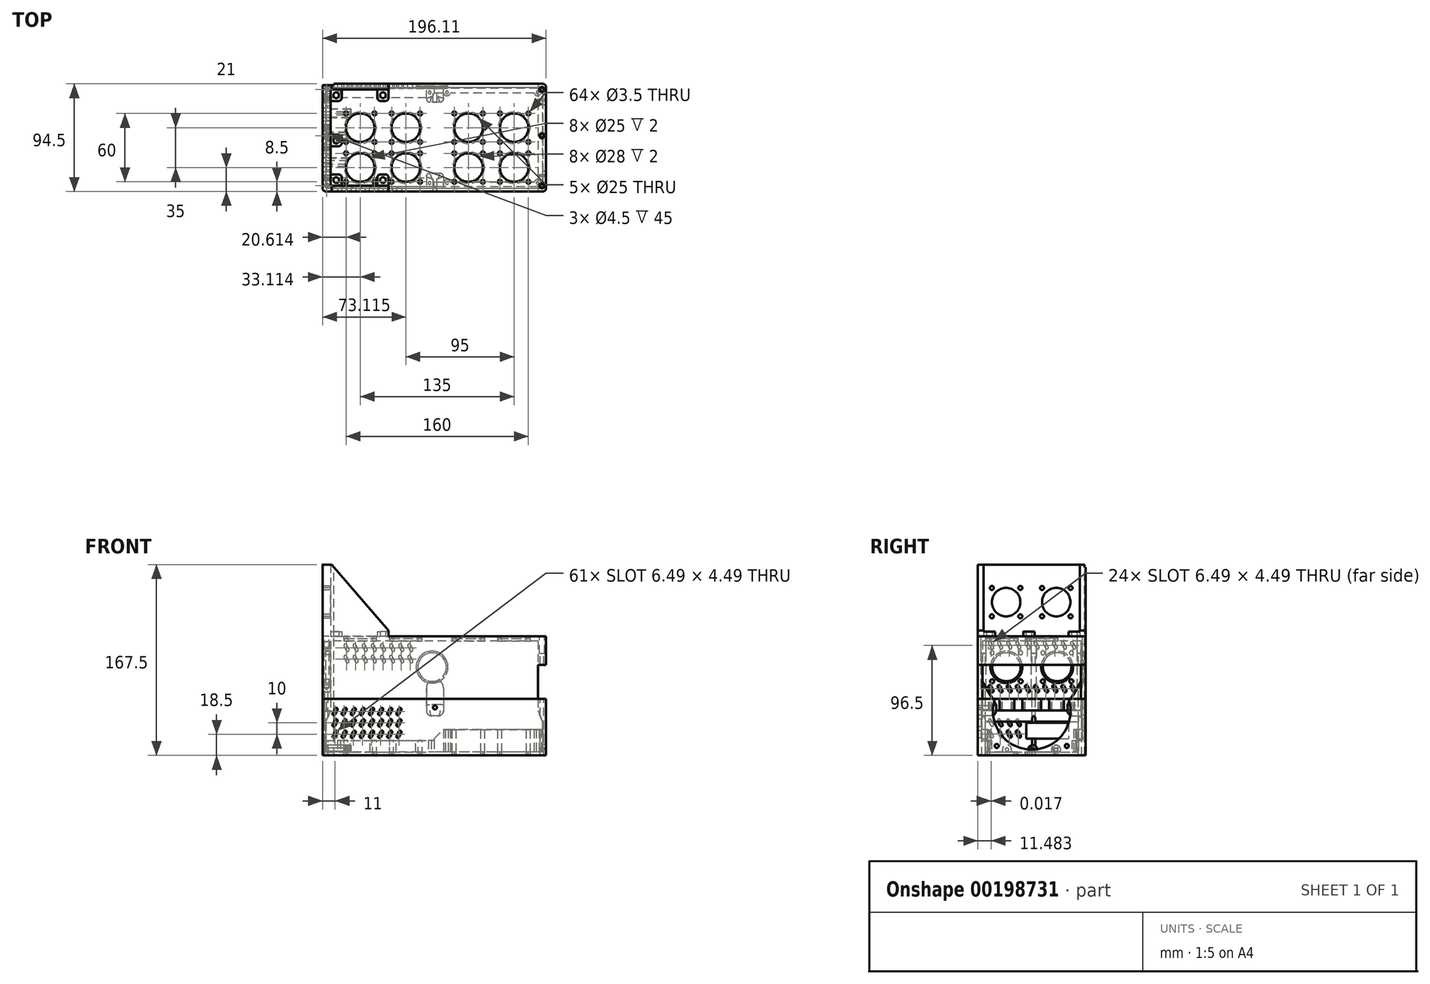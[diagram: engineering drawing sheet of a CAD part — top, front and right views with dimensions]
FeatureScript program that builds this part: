
annotation { "Feature Type Name" : "Feature", "Feature Type Description" : "" }
export const myFeature = defineFeature(function(context is Context, id is Id, definition is map)
    precondition{}
    {
        {
            var Q0;
            Q0=qCreatedBy(makeId("Top.planeOp"),FACE);
            var sketch = newSketch(context, id + "F0", { "sketchPlane" : qUnion([Q0])});
            skLineSegment(sketch, "E0.bottom", {"start": v(0, 0) * mm, "end": v(196, 0) * mm});
            skLineSegment(sketch, "E0.top", {"start": v(0, 94.5) * mm, "end": v(196, 94.5) * mm});
            skLineSegment(sketch, "E0.left", {"start": v(0, 0) * mm, "end": v(0, 94.5) * mm});
            skLineSegment(sketch, "E0.right", {"start": v(196, 0) * mm, "end": v(196, 94.5) * mm});
            skSolve(sketch);
        }
        {
            var Q0;
            Q0=qSketchRegion(id+"F0",true);
            extrude(context, id + "F1", {"entities" : qUnion([Q0]), "depth" : (3 + 10 + 36.5) * mm, "offsetDistance" : 25 * mm});
        }
        {
            var Q0;
            Q0=makeQuery(id+"F1.opExtrude","CAP_FACE",FACE,{"disambiguationData":[OSD([sQuery(id+"F0.wireOp",EDGE,"E0.bottom"),sQuery(id+"F0.wireOp",EDGE,"E0.top"),sQuery(id+"F0.wireOp",EDGE,"E0.left"),sQuery(id+"F0.wireOp",EDGE,"E0.right")])],"isStart":false});
            shell(context, id + "F2", {"entities" : qUnion([Q0]), "thickness" : 3 * mm});
        }
        {
            var Q0;
            Q0=makeQuery(id+"F2.opShell","OFFSET_FACE",FACE,{"disambiguationData":[OSD([sQuery(id+"F0.wireOp",EDGE,"E0.bottom"),sQuery(id+"F0.wireOp",EDGE,"E0.top"),sQuery(id+"F0.wireOp",EDGE,"E0.left"),sQuery(id+"F0.wireOp",EDGE,"E0.right")])]});
            var sketch = newSketch(context, id + "F3", { "sketchPlane" : qUnion([Q0])});
            skLineSegment(sketch, "E1.bottom", {"start": v(3, 3) * mm, "end": v(98, 3) * mm});
            skLineSegment(sketch, "E1.top", {"start": v(3, 12) * mm, "end": v(98, 12) * mm});
            skLineSegment(sketch, "E1.left", {"start": v(3, 3) * mm, "end": v(3, 12) * mm});
            skLineSegment(sketch, "E1.right", {"start": v(98, 3) * mm, "end": v(98, 12) * mm});
            skLineSegment(sketch, "E2.bottom", {"start": v(3, 91.5) * mm, "end": v(98, 91.5) * mm});
            skLineSegment(sketch, "E2.top", {"start": v(3, 82.5) * mm, "end": v(98, 82.5) * mm});
            skLineSegment(sketch, "E2.left", {"start": v(3, 91.5) * mm, "end": v(3, 82.5) * mm});
            skLineSegment(sketch, "E2.right", {"start": v(98, 91.5) * mm, "end": v(98, 82.5) * mm});
            skCircle(sketch, "E3", {"center": v(14.5, 87) * mm, "radius": 1.25 * mm});
            skCircle(sketch, "E4", {"center": v(94, 87) * mm, "radius": 1.25 * mm});
            skCircle(sketch, "E5", {"center": v(14.5, 7.5) * mm, "radius": 1.25 * mm});
            skCircle(sketch, "E6", {"center": v(94, 7.5) * mm, "radius": 1.25 * mm});
            skSolve(sketch);
        }
        {
            var Q0;
            Q0=qSketchRegion(id+"F3",true);
            extrude(context, id + "F4", {"entities" : qUnion([Q0]), "operationType" : NewBodyOperationType.ADD, "depth" : 10 * mm, "offsetDistance" : 25 * mm});
        }
        {
            var Q0;
            {var subQ0=sQuery(id+"F0.wireOp",EDGE,"E0.right");var subQ1=sQuery(id+"F0.wireOp",EDGE,"E0.left");var subQ2=sQuery(id+"F0.wireOp",EDGE,"E0.top");var subQ3=sQuery(id+"F0.wireOp",EDGE,"E0.bottom");Q0=makeQuery(id+"F4.boolean.opBoolean","SPLIT",FACE,{"disambiguationData":[TD([makeQuery(id+"F2.opShell","OFFSET_FACE",FACE,{"disambiguationData":[OSD([subQ3])]})])],"derivedFrom":makeQuery(id+"F2.opShell","OFFSET_FACE",FACE,{"disambiguationData":[OSD([subQ3,subQ2,subQ1,subQ0])]})});}
            var sketch = newSketch(context, id + "F5", { "sketchPlane" : qUnion([Q0])});
            skLineSegment(sketch, "E7.bottom", {"start": v(193, 3) * mm, "end": v(98, 3) * mm});
            skLineSegment(sketch, "E7.top", {"start": v(193, 8) * mm, "end": v(191.6, 8) * mm});
            skLineSegment(sketch, "E7.left", {"start": v(193, 3) * mm, "end": v(193, 8) * mm});
            skLineSegment(sketch, "E7.right", {"start": v(98, 3) * mm, "end": v(98, 8) * mm});
            skLineSegment(sketch, "E8.bottom", {"start": v(193, 91.5) * mm, "end": v(98, 91.5) * mm});
            skLineSegment(sketch, "E8.top", {"start": v(193, 86.5) * mm, "end": v(191.6, 86.5) * mm});
            skLineSegment(sketch, "E8.left", {"start": v(193, 91.5) * mm, "end": v(193, 86.5) * mm});
            skLineSegment(sketch, "E8.right", {"start": v(98, 91.5) * mm, "end": v(98, 86.5) * mm});
            skCircle(sketch, "E9", {"center": v(188.65, 87) * mm, "radius": 1.25 * mm});
            skCircle(sketch, "E10", {"center": v(109.15, 87) * mm, "radius": 1.25 * mm});
            skCircle(sketch, "E11", {"center": v(109.15, 7.5) * mm, "radius": 1.25 * mm});
            skCircle(sketch, "E12", {"center": v(188.65, 7.5) * mm, "radius": 1.25 * mm});
            skArc(sketch, "E13", {"start": v(106.2, 86.5) * mm, "mid": v(109.15, 84) * mm, "end": v(112.1, 86.5) * mm});
            skArc(sketch, "E14", {"start": v(185.7, 86.5) * mm, "mid": v(188.65, 84) * mm, "end": v(191.6, 86.5) * mm});
            skArc(sketch, "E15", {"start": v(112.1, 8) * mm, "mid": v(109.15, 10.5) * mm, "end": v(106.2, 8) * mm});
            skArc(sketch, "E16", {"start": v(191.6, 8) * mm, "mid": v(188.65, 10.5) * mm, "end": v(185.7, 8) * mm});
            skLineSegment(sketch, "E17.trimOffspring", {"start": v(106.2, 86.5) * mm, "end": v(98, 86.5) * mm});
            skLineSegment(sketch, "E18.trimOffspring", {"start": v(185.7, 86.5) * mm, "end": v(112.1, 86.5) * mm});
            skLineSegment(sketch, "E19.trimOffspring", {"start": v(185.7, 8) * mm, "end": v(112.1, 8) * mm});
            skLineSegment(sketch, "E20.trimOffspring", {"start": v(106.2, 8) * mm, "end": v(98, 8) * mm});
            skSolve(sketch);
        }
        {
            var Q0;
            Q0=qSketchRegion(id+"F5",true);
            extrude(context, id + "F6", {"entities" : qUnion([Q0]), "operationType" : NewBodyOperationType.ADD, "depth" : (10 + 1.6 + 8) * mm, "offsetDistance" : 25 * mm});
        }
        {
            var Q0;
            Q0=makeQuery(id+"F6.opExtrude","CAP_EDGE",EDGE,{"disambiguationData":[OSD([sQuery(id+"F5.wireOp",EDGE,"E8.right")])],"isStart":false});
            chamfer(context, id + "F7", {"entities" : qUnion([Q0]), "width" : 8 * mm, "tangentPropagation" : true});
        }
        {
            var Q0;
            Q0=makeQuery(id+"F6.opExtrude","CAP_EDGE",EDGE,{"disambiguationData":[OSD([sQuery(id+"F5.wireOp",EDGE,"E7.right")])],"isStart":false});
            chamfer(context, id + "F8", {"entities" : qUnion([Q0]), "width" : 8 * mm, "tangentPropagation" : true});
        }
        {
            var Q0;
            Q0=makeQuery(id+"F4.opExtrude","SWEPT_EDGE",EDGE,{"disambiguationData":[OSD([sQuery(id+"F3.wireOp",EDGE,"E2.top"),sQuery(id+"F3.wireOp",EDGE,"E2.right")])]});
            var Q1;
            Q1=makeQuery(id+"F4.opExtrude","SWEPT_EDGE",EDGE,{"disambiguationData":[OSD([sQuery(id+"F3.wireOp",EDGE,"E1.top"),sQuery(id+"F3.wireOp",EDGE,"E1.right")])]});
            fillet(context, id + "F9", {"entities" : qUnion([Q0, Q1]), "radius" : 5 * mm, "tangentPropagation" : true, "allowEdgeOverflow" : false});
        }
        {
            var Q0;
            Q0=makeQuery(id+"F2.opShell","OFFSET_FACE",FACE,{"disambiguationData":[OSD([sQuery(id+"F0.wireOp",EDGE,"E0.left")])]});
            var sketch = newSketch(context, id + "F10", { "sketchPlane" : qUnion([Q0])});
            skLineSegment(sketch, "E21.bottom", {"start": v(42.5, 28.7) * mm, "end": v(79.5, 28.7) * mm});
            skLineSegment(sketch, "E21.top", {"start": v(42.5, 14.7) * mm, "end": v(79.5, 14.7) * mm});
            skLineSegment(sketch, "E21.left", {"start": v(42.5, 28.7) * mm, "end": v(42.5, 14.7) * mm});
            skLineSegment(sketch, "E21.right", {"start": v(79.5, 28.7) * mm, "end": v(79.5, 14.7) * mm});
            skSolve(sketch);
        }
        {
            var Q0;
            Q0=qSketchRegion(id+"F10",true);
            var Q1;
            Q1=makeQuery(id+"F1.opExtrude","SWEPT_FACE",FACE,{"disambiguationData":[OSD([sQuery(id+"F0.wireOp",EDGE,"E0.left")])]});
            extrude(context, id + "F11", {"entities" : qUnion([Q0]), "operationType" : NewBodyOperationType.REMOVE, "endBound" : BoundingType.UP_TO_SURFACE, "oppositeDirection" : true, "depth" : 25 * mm, "endBoundEntityFace" : qUnion([Q1]), "offsetDistance" : 25 * mm});
        }
        {
            var Q0;
            Q0=makeQuery(id+"F2.opShell","OFFSET_FACE",FACE,{"disambiguationData":[OSD([sQuery(id+"F0.wireOp",EDGE,"E0.left")])]});
            var sketch = newSketch(context, id + "F12", { "sketchPlane" : qUnion([Q0])});
            skLineSegment(sketch, "E22.bottom", {"start": v(3, 49.5) * mm, "end": v(91.5, 49.5) * mm});
            skLineSegment(sketch, "E22.top", {"start": v(3, 29.5) * mm, "end": v(91.5, 29.5) * mm});
            skLineSegment(sketch, "E22.left", {"start": v(3, 49.5) * mm, "end": v(3, 29.5) * mm});
            skLineSegment(sketch, "E22.right", {"start": v(91.5, 49.5) * mm, "end": v(91.5, 29.5) * mm});
            skSolve(sketch);
        }
        {
            var Q0;
            Q0=qSketchRegion(id+"F12",true);
            extrude(context, id + "F13", {"entities" : qUnion([Q0]), "operationType" : NewBodyOperationType.ADD, "depth" : 4 * mm, "offsetDistance" : 25 * mm});
        }
        {
            var Q0;
            Q0=makeQuery(id+"F13.opExtrude","CAP_EDGE",EDGE,{"disambiguationData":[OSD([sQuery(id+"F12.wireOp",EDGE,"E22.top")])],"isStart":false});
            chamfer(context, id + "F14", {"entities" : qUnion([Q0]), "chamferType" : ChamferType.TWO_OFFSETS, "width1" : 10 * mm, "oppositeDirection" : false, "width2" : 4 * mm});
        }
        {
            var Q0;
            Q0=makeQuery(id+"F1.opExtrude","CAP_FACE",FACE,{"disambiguationData":[OSD([sQuery(id+"F0.wireOp",EDGE,"E0.bottom"),sQuery(id+"F0.wireOp",EDGE,"E0.top"),sQuery(id+"F0.wireOp",EDGE,"E0.left"),sQuery(id+"F0.wireOp",EDGE,"E0.right")])],"isStart":false});
            var sketch = newSketch(context, id + "F15", { "sketchPlane" : qUnion([Q0])});
            skLineSegment(sketch, "E23.bottom", {"start": v(0, 10.5) * mm, "end": v(1, 10.5) * mm});
            skLineSegment(sketch, "E23.top", {"start": v(0, 20.5) * mm, "end": v(1, 20.5) * mm});
            skLineSegment(sketch, "E23.left", {"start": v(0, 10.5) * mm, "end": v(0, 20.5) * mm});
            skLineSegment(sketch, "E23.right", {"start": v(1, 10.5) * mm, "end": v(1, 20.5) * mm});
            skLineSegment(sketch, "E24.bottom", {"start": v(1, 9.5) * mm, "end": v(3.5, 9.5) * mm});
            skLineSegment(sketch, "E24.top", {"start": v(1, 21.5) * mm, "end": v(3.5, 21.5) * mm});
            skLineSegment(sketch, "E24.left", {"start": v(1, 9.5) * mm, "end": v(1, 21.5) * mm});
            skLineSegment(sketch, "E24.right", {"start": v(3.5, 9.5) * mm, "end": v(3.5, 21.5) * mm});
            skLineSegment(sketch, "E25.bottom", {"start": v(3.5, 85) * mm, "end": v(1, 85) * mm});
            skLineSegment(sketch, "E25.top", {"start": v(3.5, 73) * mm, "end": v(1, 73) * mm});
            skLineSegment(sketch, "E25.left", {"start": v(3.5, 85) * mm, "end": v(3.5, 73) * mm});
            skLineSegment(sketch, "E25.right", {"start": v(1, 85) * mm, "end": v(1, 73) * mm});
            skLineSegment(sketch, "E26.bottom", {"start": v(0, 74) * mm, "end": v(1, 74) * mm});
            skLineSegment(sketch, "E26.top", {"start": v(0, 84) * mm, "end": v(1, 84) * mm});
            skLineSegment(sketch, "E26.left", {"start": v(0, 74) * mm, "end": v(0, 84) * mm});
            skLineSegment(sketch, "E26.right", {"start": v(1, 74) * mm, "end": v(1, 84) * mm});
            skLineSegment(sketch, "E27.bottom", {"start": v(0, 30.5) * mm, "end": v(1, 30.5) * mm});
            skLineSegment(sketch, "E27.top", {"start": v(0, 40.5) * mm, "end": v(1, 40.5) * mm});
            skLineSegment(sketch, "E27.left", {"start": v(0, 30.5) * mm, "end": v(0, 40.5) * mm});
            skLineSegment(sketch, "E27.right", {"start": v(1, 30.5) * mm, "end": v(1, 40.5) * mm});
            skLineSegment(sketch, "E28.bottom", {"start": v(0, 54) * mm, "end": v(1, 54) * mm});
            skLineSegment(sketch, "E28.top", {"start": v(0, 64) * mm, "end": v(1, 64) * mm});
            skLineSegment(sketch, "E28.left", {"start": v(0, 54) * mm, "end": v(0, 64) * mm});
            skLineSegment(sketch, "E28.right", {"start": v(1, 54) * mm, "end": v(1, 64) * mm});
            skLineSegment(sketch, "E29.bottom", {"start": v(1, 29.5) * mm, "end": v(3.5, 29.5) * mm});
            skLineSegment(sketch, "E29.top", {"start": v(1, 41.5) * mm, "end": v(3.5, 41.5) * mm});
            skLineSegment(sketch, "E29.left", {"start": v(1, 29.5) * mm, "end": v(1, 41.5) * mm});
            skLineSegment(sketch, "E29.right", {"start": v(3.5, 29.5) * mm, "end": v(3.5, 41.5) * mm});
            skLineSegment(sketch, "E30.bottom", {"start": v(1, 53) * mm, "end": v(3.5, 53) * mm});
            skLineSegment(sketch, "E30.top", {"start": v(1, 65) * mm, "end": v(3.5, 65) * mm});
            skLineSegment(sketch, "E30.left", {"start": v(1, 53) * mm, "end": v(1, 65) * mm});
            skLineSegment(sketch, "E30.right", {"start": v(3.5, 53) * mm, "end": v(3.5, 65) * mm});
            skLineSegment(sketch, "E31.bottom", {"start": v(3.5, 12) * mm, "end": v(7, 12) * mm});
            skLineSegment(sketch, "E31.top", {"start": v(3.5, 19) * mm, "end": v(7, 19) * mm});
            skLineSegment(sketch, "E31.left", {"start": v(3.5, 12) * mm, "end": v(3.5, 19) * mm});
            skLineSegment(sketch, "E31.right", {"start": v(7, 12) * mm, "end": v(7, 19) * mm});
            skLineSegment(sketch, "E32.bottom", {"start": v(3.5, 32) * mm, "end": v(7, 32) * mm});
            skLineSegment(sketch, "E32.top", {"start": v(3.5, 39) * mm, "end": v(7, 39) * mm});
            skLineSegment(sketch, "E32.left", {"start": v(3.5, 32) * mm, "end": v(3.5, 39) * mm});
            skLineSegment(sketch, "E32.right", {"start": v(7, 32) * mm, "end": v(7, 39) * mm});
            skLineSegment(sketch, "E33.bottom", {"start": v(3.5, 55.5) * mm, "end": v(7, 55.5) * mm});
            skLineSegment(sketch, "E33.top", {"start": v(3.5, 62.5) * mm, "end": v(7, 62.5) * mm});
            skLineSegment(sketch, "E33.left", {"start": v(3.5, 55.5) * mm, "end": v(3.5, 62.5) * mm});
            skLineSegment(sketch, "E33.right", {"start": v(7, 55.5) * mm, "end": v(7, 62.5) * mm});
            skLineSegment(sketch, "E34.bottom", {"start": v(3.5, 75.5) * mm, "end": v(7, 75.5) * mm});
            skLineSegment(sketch, "E34.top", {"start": v(3.5, 82.5) * mm, "end": v(7, 82.5) * mm});
            skLineSegment(sketch, "E34.left", {"start": v(3.5, 75.5) * mm, "end": v(3.5, 82.5) * mm});
            skLineSegment(sketch, "E34.right", {"start": v(7, 75.5) * mm, "end": v(7, 82.5) * mm});
            skSolve(sketch);
        }
        {
            var Q0;
            Q0=qSketchRegion(id+"F15",true);
            extrude(context, id + "F16", {"entities" : qUnion([Q0]), "operationType" : NewBodyOperationType.REMOVE, "oppositeDirection" : true, "depth" : 10 * mm, "offsetDistance" : 25 * mm});
        }
        {
            var Q0;
            Q0=makeQuery(id+"F2.opShell","OFFSET_FACE",FACE,{"disambiguationData":[OSD([sQuery(id+"F0.wireOp",EDGE,"E0.right")])]});
            var sketch = newSketch(context, id + "F17", { "sketchPlane" : qUnion([Q0])});
            skLineSegment(sketch, "E35.bottom", {"start": v(-91.5, 49.5) * mm, "end": v(-3, 49.5) * mm});
            skLineSegment(sketch, "E35.top", {"start": v(-91.5, 29.5) * mm, "end": v(-3, 29.5) * mm});
            skLineSegment(sketch, "E35.left", {"start": v(-91.5, 49.5) * mm, "end": v(-91.5, 29.5) * mm});
            skLineSegment(sketch, "E35.right", {"start": v(-3, 49.5) * mm, "end": v(-3, 29.5) * mm});
            skSolve(sketch);
        }
        {
            var Q0;
            Q0=qSketchRegion(id+"F17",true);
            extrude(context, id + "F18", {"entities" : qUnion([Q0]), "operationType" : NewBodyOperationType.ADD, "depth" : 4 * mm, "offsetDistance" : 25 * mm});
        }
        {
            var Q0;
            Q0=makeQuery(id+"F18.opExtrude","CAP_EDGE",EDGE,{"disambiguationData":[OSD([sQuery(id+"F17.wireOp",EDGE,"E35.top")])],"isStart":false});
            chamfer(context, id + "F19", {"entities" : qUnion([Q0]), "chamferType" : ChamferType.TWO_OFFSETS, "width1" : 10 * mm, "oppositeDirection" : false, "width2" : 4 * mm, "tangentPropagation" : true});
        }
        {
            var Q0;
            {var subQ1=sQuery(id+"F12.wireOp",EDGE,"E22.bottom");var subQ3=sQuery(id+"F0.wireOp",EDGE,"E0.bottom");var subQ4=sQuery(id+"F0.wireOp",EDGE,"E0.right");var subQ5=sQuery(id+"F0.wireOp",EDGE,"E0.top");var subQ9=sQuery(id+"F0.wireOp",EDGE,"E0.left");Q0=makeQuery(id+"F18.boolean.opBoolean","MERGE",FACE,{"derivedFrom":[makeQuery(id+"F16.boolean.opBoolean","SPLIT",FACE,{"disambiguationData":[TD([makeQuery(id+"F1.opExtrude","SWEPT_FACE",FACE,{"disambiguationData":[OSD([subQ3])]})])],"derivedFrom":makeQuery(id+"F13.boolean.opBoolean","MERGE",FACE,{"derivedFrom":[makeQuery(id+"F1.opExtrude","CAP_FACE",FACE,{"disambiguationData":[OSD([subQ3,subQ5,subQ9,subQ4])],"isStart":false}),makeQuery(id+"F13.opExtrude","SWEPT_FACE",FACE,{"disambiguationData":[OSD([subQ1])]})]})}),makeQuery(id+"F18.opExtrude","SWEPT_FACE",FACE,{"disambiguationData":[OSD([sQuery(id+"F17.wireOp",EDGE,"E35.bottom")])]})]});}
            var sketch = newSketch(context, id + "F20", { "sketchPlane" : qUnion([Q0])});
            skCircle(sketch, "E36", {"center": v(192.5, 89.5) * mm, "radius": 1.5 * mm});
            skCircle(sketch, "E37", {"center": v(192.5, 5) * mm, "radius": 1.5 * mm});
            skCircle(sketch, "E38", {"center": v(3.5, 89.5) * mm, "radius": 1.5 * mm});
            skCircle(sketch, "E39", {"center": v(3.5, 5) * mm, "radius": 1.5 * mm});
            skCircle(sketch, "E40", {"center": v(3.5, 49) * mm, "radius": 1.5 * mm});
            skCircle(sketch, "E41", {"center": v(192.5, 49) * mm, "radius": 1.5 * mm});
            skSolve(sketch);
        }
        {
            var Q0;
            Q0=qSketchRegion(id+"F20",true);
            extrude(context, id + "F21", {"entities" : qUnion([Q0]), "operationType" : NewBodyOperationType.REMOVE, "oppositeDirection" : true, "depth" : 12 * mm, "offsetDistance" : 25 * mm});
        }
        {
            var Q0;
            {var subQ1=sQuery(id+"F12.wireOp",EDGE,"E22.bottom");var subQ3=sQuery(id+"F0.wireOp",EDGE,"E0.bottom");var subQ4=sQuery(id+"F0.wireOp",EDGE,"E0.right");var subQ5=sQuery(id+"F0.wireOp",EDGE,"E0.top");var subQ9=sQuery(id+"F0.wireOp",EDGE,"E0.left");Q0=makeQuery(id+"F18.boolean.opBoolean","MERGE",FACE,{"derivedFrom":[makeQuery(id+"F16.boolean.opBoolean","SPLIT",FACE,{"disambiguationData":[TD([makeQuery(id+"F1.opExtrude","SWEPT_FACE",FACE,{"disambiguationData":[OSD([subQ3])]})])],"derivedFrom":makeQuery(id+"F13.boolean.opBoolean","MERGE",FACE,{"derivedFrom":[makeQuery(id+"F1.opExtrude","CAP_FACE",FACE,{"disambiguationData":[OSD([subQ3,subQ5,subQ9,subQ4])],"isStart":false}),makeQuery(id+"F13.opExtrude","SWEPT_FACE",FACE,{"disambiguationData":[OSD([subQ1])]})]})}),makeQuery(id+"F18.opExtrude","SWEPT_FACE",FACE,{"disambiguationData":[OSD([sQuery(id+"F17.wireOp",EDGE,"E35.bottom")])]})]});}
            var sketch = newSketch(context, id + "F22", { "sketchPlane" : qUnion([Q0])});
            skLineSegment(sketch, "E42.bottom", {"start": v(0, 94.5) * mm, "end": v(10, 94.5) * mm});
            skLineSegment(sketch, "E42.top", {"start": v(0, 93.5) * mm, "end": v(10, 93.5) * mm});
            skLineSegment(sketch, "E42.left", {"start": v(0, 94.5) * mm, "end": v(0, 93.5) * mm});
            skLineSegment(sketch, "E42.right", {"start": v(10, 94.5) * mm, "end": v(10, 93.5) * mm});
            skSolve(sketch);
        }
        {
            var Q0;
            Q0=makeQuery(id+"F22.imprint","IMPRINT",FACE,{"disambiguationData":[TD([[makeQuery(id+"F22.imprint","IMPRINT",EDGE,{"derivedFrom":sQuery(id+"F22.wireOp",EDGE,"E42.bottom")}),-1.0]])]});
            var Q1;
            Q1=makeQuery(id+"F1.opExtrude","CAP_FACE",FACE,{"disambiguationData":[OSD([sQuery(id+"F0.wireOp",EDGE,"E0.bottom"),sQuery(id+"F0.wireOp",EDGE,"E0.top"),sQuery(id+"F0.wireOp",EDGE,"E0.left"),sQuery(id+"F0.wireOp",EDGE,"E0.right")])],"isStart":true});
            extrude(context, id + "F23", {"entities" : qUnion([Q0]), "operationType" : NewBodyOperationType.REMOVE, "endBound" : BoundingType.UP_TO_SURFACE, "oppositeDirection" : true, "depth" : 25 * mm, "endBoundEntityFace" : qUnion([Q1]), "offsetDistance" : 25 * mm});
        }
        {
            var Q0;
            Q0=makeQuery(id+"F1.opExtrude","SWEPT_FACE",FACE,{"disambiguationData":[OSD([sQuery(id+"F0.wireOp",EDGE,"E0.left")])]});
            var sketch = newSketch(context, id + "F24", { "sketchPlane" : qUnion([Q0])});
            skCircle(sketch, "E43", {"center": v(-25.5, 5) * mm, "radius": 1.5 * mm});
            skCircle(sketch, "E44", {"center": v(-48, 5) * mm, "radius": 1.5 * mm});
            skCircle(sketch, "E45", {"center": v(-68.5, 5) * mm, "radius": 1.5 * mm});
            skCircle(sketch, "E46", {"center": v(-25.5, 5) * mm, "radius": 4 * mm});
            skCircle(sketch, "E47", {"center": v(-48, 5) * mm, "radius": 4 * mm});
            skCircle(sketch, "E48", {"center": v(-68.5, 5) * mm, "radius": 4 * mm});
            skSolve(sketch);
        }
        {
            var Q0;
            Q0=qSketchRegion(id+"F24",true);
            extrude(context, id + "F25", {"entities" : qUnion([Q0]), "operationType" : NewBodyOperationType.ADD, "oppositeDirection" : true, "depth" : 25 * mm, "offsetDistance" : 25 * mm});
        }
        {
            var Q0;
            Q0=makeQuery(id+"F24.imprint","IMPRINT",FACE,{"disambiguationData":[TD([[makeQuery(id+"F24.imprint","IMPRINT",EDGE,{"derivedFrom":sQuery(id+"F24.wireOp",EDGE,"E45")}),1.0]])]});
            var Q1;
            Q1=makeQuery(id+"F24.imprint","IMPRINT",FACE,{"disambiguationData":[TD([[makeQuery(id+"F24.imprint","IMPRINT",EDGE,{"derivedFrom":sQuery(id+"F24.wireOp",EDGE,"E44")}),1.0]])]});
            var Q2;
            Q2=makeQuery(id+"F24.imprint","IMPRINT",FACE,{"disambiguationData":[TD([[makeQuery(id+"F24.imprint","IMPRINT",EDGE,{"derivedFrom":sQuery(id+"F24.wireOp",EDGE,"E43")}),1.0]])]});
            extrude(context, id + "F26", {"entities" : qUnion([Q0, Q1, Q2]), "operationType" : NewBodyOperationType.REMOVE, "oppositeDirection" : true, "depth" : 23 * mm, "offsetDistance" : 25 * mm});
        }
        {
            var Q0;
            Q0=makeQuery(id+"F1.opExtrude","SWEPT_FACE",FACE,{"disambiguationData":[OSD([sQuery(id+"F0.wireOp",EDGE,"E0.bottom")])]});
            var sketch = newSketch(context, id + "F27", { "sketchPlane" : qUnion([Q0])});
            skArc(sketch, "E49", {"start": v(8.88, 17.06) * mm, "mid": v(9.44, 15.38) * mm, "end": v(11.12, 15.94) * mm});
            skArc(sketch, "E50", {"start": v(13.12, 19.94) * mm, "mid": v(12.56, 21.62) * mm, "end": v(10.88, 21.06) * mm});
            skLineSegment(sketch, "E51", {"start": v(10.88, 21.06) * mm, "end": v(8.88, 17.06) * mm});
            skLineSegment(sketch, "E52", {"start": v(13.12, 19.94) * mm, "end": v(11.12, 15.94) * mm});
            skArc(sketch, "E53.0.1.0", {"start": v(13.12, 29.94) * mm, "mid": v(12.56, 31.62) * mm, "end": v(10.88, 31.06) * mm});
            skLineSegment(sketch, "E53.0.1.1", {"start": v(10.88, 31.06) * mm, "end": v(8.88, 27.06) * mm});
            skArc(sketch, "E53.0.1.2", {"start": v(8.88, 27.06) * mm, "mid": v(9.44, 25.38) * mm, "end": v(11.12, 25.94) * mm});
            skLineSegment(sketch, "E53.0.1.3", {"start": v(13.12, 29.94) * mm, "end": v(11.12, 25.94) * mm});
            skArc(sketch, "E53.0.2.0", {"start": v(13.12, 39.94) * mm, "mid": v(12.56, 41.62) * mm, "end": v(10.88, 41.06) * mm});
            skLineSegment(sketch, "E53.0.2.1", {"start": v(10.88, 41.06) * mm, "end": v(8.88, 37.06) * mm});
            skArc(sketch, "E53.0.2.2", {"start": v(8.88, 37.06) * mm, "mid": v(9.44, 35.38) * mm, "end": v(11.12, 35.94) * mm});
            skLineSegment(sketch, "E53.0.2.3", {"start": v(13.12, 39.94) * mm, "end": v(11.12, 35.94) * mm});
            skArc(sketch, "E53.1.0.0", {"start": v(21.12, 19.94) * mm, "mid": v(20.56, 21.62) * mm, "end": v(18.88, 21.06) * mm});
            skLineSegment(sketch, "E53.1.0.1", {"start": v(18.88, 21.06) * mm, "end": v(16.88, 17.06) * mm});
            skArc(sketch, "E53.1.0.2", {"start": v(16.88, 17.06) * mm, "mid": v(17.44, 15.38) * mm, "end": v(19.12, 15.94) * mm});
            skLineSegment(sketch, "E53.1.0.3", {"start": v(21.12, 19.94) * mm, "end": v(19.12, 15.94) * mm});
            skArc(sketch, "E53.1.1.0", {"start": v(21.12, 29.94) * mm, "mid": v(20.56, 31.62) * mm, "end": v(18.88, 31.06) * mm});
            skLineSegment(sketch, "E53.1.1.1", {"start": v(18.88, 31.06) * mm, "end": v(16.88, 27.06) * mm});
            skArc(sketch, "E53.1.1.2", {"start": v(16.88, 27.06) * mm, "mid": v(17.44, 25.38) * mm, "end": v(19.12, 25.94) * mm});
            skLineSegment(sketch, "E53.1.1.3", {"start": v(21.12, 29.94) * mm, "end": v(19.12, 25.94) * mm});
            skArc(sketch, "E53.1.2.0", {"start": v(21.12, 39.94) * mm, "mid": v(20.56, 41.62) * mm, "end": v(18.88, 41.06) * mm});
            skLineSegment(sketch, "E53.1.2.1", {"start": v(18.88, 41.06) * mm, "end": v(16.88, 37.06) * mm});
            skArc(sketch, "E53.1.2.2", {"start": v(16.88, 37.06) * mm, "mid": v(17.44, 35.38) * mm, "end": v(19.12, 35.94) * mm});
            skLineSegment(sketch, "E53.1.2.3", {"start": v(21.12, 39.94) * mm, "end": v(19.12, 35.94) * mm});
            skArc(sketch, "E53.2.0.0", {"start": v(29.12, 19.94) * mm, "mid": v(28.56, 21.62) * mm, "end": v(26.88, 21.06) * mm});
            skLineSegment(sketch, "E53.2.0.1", {"start": v(26.88, 21.06) * mm, "end": v(24.88, 17.06) * mm});
            skArc(sketch, "E53.2.0.2", {"start": v(24.88, 17.06) * mm, "mid": v(25.44, 15.38) * mm, "end": v(27.12, 15.94) * mm});
            skLineSegment(sketch, "E53.2.0.3", {"start": v(29.12, 19.94) * mm, "end": v(27.12, 15.94) * mm});
            skArc(sketch, "E53.2.1.0", {"start": v(29.12, 29.94) * mm, "mid": v(28.56, 31.62) * mm, "end": v(26.88, 31.06) * mm});
            skLineSegment(sketch, "E53.2.1.1", {"start": v(26.88, 31.06) * mm, "end": v(24.88, 27.06) * mm});
            skArc(sketch, "E53.2.1.2", {"start": v(24.88, 27.06) * mm, "mid": v(25.44, 25.38) * mm, "end": v(27.12, 25.94) * mm});
            skLineSegment(sketch, "E53.2.1.3", {"start": v(29.12, 29.94) * mm, "end": v(27.12, 25.94) * mm});
            skArc(sketch, "E53.2.2.0", {"start": v(29.12, 39.94) * mm, "mid": v(28.56, 41.62) * mm, "end": v(26.88, 41.06) * mm});
            skLineSegment(sketch, "E53.2.2.1", {"start": v(26.88, 41.06) * mm, "end": v(24.88, 37.06) * mm});
            skArc(sketch, "E53.2.2.2", {"start": v(24.88, 37.06) * mm, "mid": v(25.44, 35.38) * mm, "end": v(27.12, 35.94) * mm});
            skLineSegment(sketch, "E53.2.2.3", {"start": v(29.12, 39.94) * mm, "end": v(27.12, 35.94) * mm});
            skArc(sketch, "E53.3.0.0", {"start": v(37.12, 19.94) * mm, "mid": v(36.56, 21.62) * mm, "end": v(34.88, 21.06) * mm});
            skLineSegment(sketch, "E53.3.0.1", {"start": v(34.88, 21.06) * mm, "end": v(32.88, 17.06) * mm});
            skArc(sketch, "E53.3.0.2", {"start": v(32.88, 17.06) * mm, "mid": v(33.44, 15.38) * mm, "end": v(35.12, 15.94) * mm});
            skLineSegment(sketch, "E53.3.0.3", {"start": v(37.12, 19.94) * mm, "end": v(35.12, 15.94) * mm});
            skArc(sketch, "E53.3.1.0", {"start": v(37.12, 29.94) * mm, "mid": v(36.56, 31.62) * mm, "end": v(34.88, 31.06) * mm});
            skLineSegment(sketch, "E53.3.1.1", {"start": v(34.88, 31.06) * mm, "end": v(32.88, 27.06) * mm});
            skArc(sketch, "E53.3.1.2", {"start": v(32.88, 27.06) * mm, "mid": v(33.44, 25.38) * mm, "end": v(35.12, 25.94) * mm});
            skLineSegment(sketch, "E53.3.1.3", {"start": v(37.12, 29.94) * mm, "end": v(35.12, 25.94) * mm});
            skArc(sketch, "E53.3.2.0", {"start": v(37.12, 39.94) * mm, "mid": v(36.56, 41.62) * mm, "end": v(34.88, 41.06) * mm});
            skLineSegment(sketch, "E53.3.2.1", {"start": v(34.88, 41.06) * mm, "end": v(32.88, 37.06) * mm});
            skArc(sketch, "E53.3.2.2", {"start": v(32.88, 37.06) * mm, "mid": v(33.44, 35.38) * mm, "end": v(35.12, 35.94) * mm});
            skLineSegment(sketch, "E53.3.2.3", {"start": v(37.12, 39.94) * mm, "end": v(35.12, 35.94) * mm});
            skArc(sketch, "E53.4.0.0", {"start": v(45.12, 19.94) * mm, "mid": v(44.56, 21.62) * mm, "end": v(42.88, 21.06) * mm});
            skLineSegment(sketch, "E53.4.0.1", {"start": v(42.88, 21.06) * mm, "end": v(40.88, 17.06) * mm});
            skArc(sketch, "E53.4.0.2", {"start": v(40.88, 17.06) * mm, "mid": v(41.44, 15.38) * mm, "end": v(43.12, 15.94) * mm});
            skLineSegment(sketch, "E53.4.0.3", {"start": v(45.12, 19.94) * mm, "end": v(43.12, 15.94) * mm});
            skArc(sketch, "E53.4.1.0", {"start": v(45.12, 29.94) * mm, "mid": v(44.56, 31.62) * mm, "end": v(42.88, 31.06) * mm});
            skLineSegment(sketch, "E53.4.1.1", {"start": v(42.88, 31.06) * mm, "end": v(40.88, 27.06) * mm});
            skArc(sketch, "E53.4.1.2", {"start": v(40.88, 27.06) * mm, "mid": v(41.44, 25.38) * mm, "end": v(43.12, 25.94) * mm});
            skLineSegment(sketch, "E53.4.1.3", {"start": v(45.12, 29.94) * mm, "end": v(43.12, 25.94) * mm});
            skArc(sketch, "E53.4.2.0", {"start": v(45.12, 39.94) * mm, "mid": v(44.56, 41.62) * mm, "end": v(42.88, 41.06) * mm});
            skLineSegment(sketch, "E53.4.2.1", {"start": v(42.88, 41.06) * mm, "end": v(40.88, 37.06) * mm});
            skArc(sketch, "E53.4.2.2", {"start": v(40.88, 37.06) * mm, "mid": v(41.44, 35.38) * mm, "end": v(43.12, 35.94) * mm});
            skLineSegment(sketch, "E53.4.2.3", {"start": v(45.12, 39.94) * mm, "end": v(43.12, 35.94) * mm});
            skArc(sketch, "E53.5.0.0", {"start": v(53.12, 19.94) * mm, "mid": v(52.56, 21.62) * mm, "end": v(50.88, 21.06) * mm});
            skLineSegment(sketch, "E53.5.0.1", {"start": v(50.88, 21.06) * mm, "end": v(48.88, 17.06) * mm});
            skArc(sketch, "E53.5.0.2", {"start": v(48.88, 17.06) * mm, "mid": v(49.44, 15.38) * mm, "end": v(51.12, 15.94) * mm});
            skLineSegment(sketch, "E53.5.0.3", {"start": v(53.12, 19.94) * mm, "end": v(51.12, 15.94) * mm});
            skArc(sketch, "E53.5.1.0", {"start": v(53.12, 29.94) * mm, "mid": v(52.56, 31.62) * mm, "end": v(50.88, 31.06) * mm});
            skLineSegment(sketch, "E53.5.1.1", {"start": v(50.88, 31.06) * mm, "end": v(48.88, 27.06) * mm});
            skArc(sketch, "E53.5.1.2", {"start": v(48.88, 27.06) * mm, "mid": v(49.44, 25.38) * mm, "end": v(51.12, 25.94) * mm});
            skLineSegment(sketch, "E53.5.1.3", {"start": v(53.12, 29.94) * mm, "end": v(51.12, 25.94) * mm});
            skArc(sketch, "E53.5.2.0", {"start": v(53.12, 39.94) * mm, "mid": v(52.56, 41.62) * mm, "end": v(50.88, 41.06) * mm});
            skLineSegment(sketch, "E53.5.2.1", {"start": v(50.88, 41.06) * mm, "end": v(48.88, 37.06) * mm});
            skArc(sketch, "E53.5.2.2", {"start": v(48.88, 37.06) * mm, "mid": v(49.44, 35.38) * mm, "end": v(51.12, 35.94) * mm});
            skLineSegment(sketch, "E53.5.2.3", {"start": v(53.12, 39.94) * mm, "end": v(51.12, 35.94) * mm});
            skLineSegment(sketch, "E53.direction1", {"start": v(8.88, 17.06) * mm, "end": v(16.88, 17.06) * mm, "construction": true});
            skLineSegment(sketch, "E53.direction2", {"start": v(8.88, 17.06) * mm, "end": v(8.88, 27.06) * mm, "construction": true});
            skArc(sketch, "E54.0.6.0", {"start": v(61.12, 19.94) * mm, "mid": v(60.56, 21.62) * mm, "end": v(58.88, 21.06) * mm});
            skLineSegment(sketch, "E54.4.6.0", {"start": v(58.88, 21.06) * mm, "end": v(56.88, 17.06) * mm});
            skArc(sketch, "E54.7.6.0", {"start": v(56.88, 17.06) * mm, "mid": v(57.44, 15.38) * mm, "end": v(59.12, 15.94) * mm});
            skLineSegment(sketch, "E54.11.6.0", {"start": v(61.12, 19.94) * mm, "end": v(59.12, 15.94) * mm});
            skArc(sketch, "E54.0.6.1", {"start": v(61.12, 29.94) * mm, "mid": v(60.56, 31.62) * mm, "end": v(58.88, 31.06) * mm});
            skLineSegment(sketch, "E54.4.6.1", {"start": v(58.88, 31.06) * mm, "end": v(56.88, 27.06) * mm});
            skArc(sketch, "E54.7.6.1", {"start": v(56.88, 27.06) * mm, "mid": v(57.44, 25.38) * mm, "end": v(59.12, 25.94) * mm});
            skLineSegment(sketch, "E54.11.6.1", {"start": v(61.12, 29.94) * mm, "end": v(59.12, 25.94) * mm});
            skArc(sketch, "E54.0.6.2", {"start": v(61.12, 39.94) * mm, "mid": v(60.56, 41.62) * mm, "end": v(58.88, 41.06) * mm});
            skLineSegment(sketch, "E54.4.6.2", {"start": v(58.88, 41.06) * mm, "end": v(56.88, 37.06) * mm});
            skArc(sketch, "E54.7.6.2", {"start": v(56.88, 37.06) * mm, "mid": v(57.44, 35.38) * mm, "end": v(59.12, 35.94) * mm});
            skLineSegment(sketch, "E54.11.6.2", {"start": v(61.12, 39.94) * mm, "end": v(59.12, 35.94) * mm});
            skArc(sketch, "E54.0.7.0", {"start": v(69.12, 19.94) * mm, "mid": v(68.56, 21.62) * mm, "end": v(66.88, 21.06) * mm});
            skLineSegment(sketch, "E54.4.7.0", {"start": v(66.88, 21.06) * mm, "end": v(64.88, 17.06) * mm});
            skArc(sketch, "E54.7.7.0", {"start": v(64.88, 17.06) * mm, "mid": v(65.44, 15.38) * mm, "end": v(67.12, 15.94) * mm});
            skLineSegment(sketch, "E54.11.7.0", {"start": v(69.12, 19.94) * mm, "end": v(67.12, 15.94) * mm});
            skArc(sketch, "E54.0.7.1", {"start": v(69.12, 29.94) * mm, "mid": v(68.56, 31.62) * mm, "end": v(66.88, 31.06) * mm});
            skLineSegment(sketch, "E54.4.7.1", {"start": v(66.88, 31.06) * mm, "end": v(64.88, 27.06) * mm});
            skArc(sketch, "E54.7.7.1", {"start": v(64.88, 27.06) * mm, "mid": v(65.44, 25.38) * mm, "end": v(67.12, 25.94) * mm});
            skLineSegment(sketch, "E54.11.7.1", {"start": v(69.12, 29.94) * mm, "end": v(67.12, 25.94) * mm});
            skArc(sketch, "E54.0.7.2", {"start": v(69.12, 39.94) * mm, "mid": v(68.56, 41.62) * mm, "end": v(66.88, 41.06) * mm});
            skLineSegment(sketch, "E54.4.7.2", {"start": v(66.88, 41.06) * mm, "end": v(64.88, 37.06) * mm});
            skArc(sketch, "E54.7.7.2", {"start": v(64.88, 37.06) * mm, "mid": v(65.44, 35.38) * mm, "end": v(67.12, 35.94) * mm});
            skLineSegment(sketch, "E54.11.7.2", {"start": v(69.12, 39.94) * mm, "end": v(67.12, 35.94) * mm});
            skSolve(sketch);
        }
        {
            var Q0;
            Q0=qSketchRegion(id+"F27",true);
            var Q1;
            Q1=makeQuery(id+"F1.opExtrude","SWEPT_FACE",FACE,{"disambiguationData":[OSD([sQuery(id+"F0.wireOp",EDGE,"E0.top")])]});
            extrude(context, id + "F28", {"entities" : qUnion([Q0]), "operationType" : NewBodyOperationType.REMOVE, "endBound" : BoundingType.UP_TO_SURFACE, "oppositeDirection" : true, "depth" : 25 * mm, "endBoundEntityFace" : qUnion([Q1]), "offsetDistance" : 25 * mm});
        }
        {
            var Q0;
            Q0=makeQuery(id+"F1.opExtrude","SWEPT_FACE",FACE,{"disambiguationData":[OSD([sQuery(id+"F0.wireOp",EDGE,"E0.left")])]});
            var sketch = newSketch(context, id + "F29", { "sketchPlane" : qUnion([Q0])});
            skArc(sketch, "E55", {"start": v(-37.62, 17.26) * mm, "mid": v(-37.06, 15.58) * mm, "end": v(-35.38, 16.14) * mm});
            skArc(sketch, "E56", {"start": v(-33.38, 20.14) * mm, "mid": v(-33.94, 21.82) * mm, "end": v(-35.62, 21.26) * mm});
            skLineSegment(sketch, "E57", {"start": v(-35.62, 21.26) * mm, "end": v(-37.62, 17.26) * mm});
            skLineSegment(sketch, "E58", {"start": v(-33.38, 20.14) * mm, "end": v(-35.38, 16.14) * mm});
            skArc(sketch, "E59.0.1.0", {"start": v(-33.38, 30.14) * mm, "mid": v(-33.94, 31.82) * mm, "end": v(-35.62, 31.26) * mm});
            skLineSegment(sketch, "E59.0.1.1", {"start": v(-35.62, 31.26) * mm, "end": v(-37.62, 27.26) * mm});
            skLineSegment(sketch, "E59.0.1.2", {"start": v(-33.38, 30.14) * mm, "end": v(-35.38, 26.14) * mm});
            skArc(sketch, "E59.0.1.3", {"start": v(-37.62, 27.26) * mm, "mid": v(-37.06, 25.58) * mm, "end": v(-35.38, 26.14) * mm});
            skArc(sketch, "E59.1.0.0", {"start": v(-25.38, 20.14) * mm, "mid": v(-25.94, 21.82) * mm, "end": v(-27.62, 21.26) * mm});
            skLineSegment(sketch, "E59.1.0.1", {"start": v(-27.62, 21.26) * mm, "end": v(-29.62, 17.26) * mm});
            skLineSegment(sketch, "E59.1.0.2", {"start": v(-25.38, 20.14) * mm, "end": v(-27.38, 16.14) * mm});
            skArc(sketch, "E59.1.0.3", {"start": v(-29.62, 17.26) * mm, "mid": v(-29.06, 15.58) * mm, "end": v(-27.38, 16.14) * mm});
            skArc(sketch, "E59.1.1.0", {"start": v(-25.38, 30.14) * mm, "mid": v(-25.94, 31.82) * mm, "end": v(-27.62, 31.26) * mm});
            skLineSegment(sketch, "E59.1.1.1", {"start": v(-27.62, 31.26) * mm, "end": v(-29.62, 27.26) * mm});
            skLineSegment(sketch, "E59.1.1.2", {"start": v(-25.38, 30.14) * mm, "end": v(-27.38, 26.14) * mm});
            skArc(sketch, "E59.1.1.3", {"start": v(-29.62, 27.26) * mm, "mid": v(-29.06, 25.58) * mm, "end": v(-27.38, 26.14) * mm});
            skArc(sketch, "E59.2.0.0", {"start": v(-17.38, 20.14) * mm, "mid": v(-17.94, 21.82) * mm, "end": v(-19.62, 21.26) * mm});
            skLineSegment(sketch, "E59.2.0.1", {"start": v(-19.62, 21.26) * mm, "end": v(-21.62, 17.26) * mm});
            skLineSegment(sketch, "E59.2.0.2", {"start": v(-17.38, 20.14) * mm, "end": v(-19.38, 16.14) * mm});
            skArc(sketch, "E59.2.0.3", {"start": v(-21.62, 17.26) * mm, "mid": v(-21.06, 15.58) * mm, "end": v(-19.38, 16.14) * mm});
            skArc(sketch, "E59.2.1.0", {"start": v(-17.38, 30.14) * mm, "mid": v(-17.94, 31.82) * mm, "end": v(-19.62, 31.26) * mm});
            skLineSegment(sketch, "E59.2.1.1", {"start": v(-19.62, 31.26) * mm, "end": v(-21.62, 27.26) * mm});
            skLineSegment(sketch, "E59.2.1.2", {"start": v(-17.38, 30.14) * mm, "end": v(-19.38, 26.14) * mm});
            skArc(sketch, "E59.2.1.3", {"start": v(-21.62, 27.26) * mm, "mid": v(-21.06, 25.58) * mm, "end": v(-19.38, 26.14) * mm});
            skArc(sketch, "E59.3.0.0", {"start": v(-9.38, 20.14) * mm, "mid": v(-9.94, 21.82) * mm, "end": v(-11.62, 21.26) * mm});
            skLineSegment(sketch, "E59.3.0.1", {"start": v(-11.62, 21.26) * mm, "end": v(-13.62, 17.26) * mm});
            skLineSegment(sketch, "E59.3.0.2", {"start": v(-9.38, 20.14) * mm, "end": v(-11.38, 16.14) * mm});
            skArc(sketch, "E59.3.0.3", {"start": v(-13.62, 17.26) * mm, "mid": v(-13.06, 15.58) * mm, "end": v(-11.38, 16.14) * mm});
            skArc(sketch, "E59.3.1.0", {"start": v(-9.38, 30.14) * mm, "mid": v(-9.94, 31.82) * mm, "end": v(-11.62, 31.26) * mm});
            skLineSegment(sketch, "E59.3.1.1", {"start": v(-11.62, 31.26) * mm, "end": v(-13.62, 27.26) * mm});
            skLineSegment(sketch, "E59.3.1.2", {"start": v(-9.38, 30.14) * mm, "end": v(-11.38, 26.14) * mm});
            skArc(sketch, "E59.3.1.3", {"start": v(-13.62, 27.26) * mm, "mid": v(-13.06, 25.58) * mm, "end": v(-11.38, 26.14) * mm});
            skLineSegment(sketch, "E59.direction1", {"start": v(-35.62, 21.26) * mm, "end": v(-27.62, 21.26) * mm, "construction": true});
            skLineSegment(sketch, "E59.direction2", {"start": v(-35.62, 21.26) * mm, "end": v(-35.62, 31.26) * mm, "construction": true});
            skSolve(sketch);
        }
        {
            var Q0;
            Q0=qSketchRegion(id+"F29",true);
            var Q1;
            {var subQ2=sQuery(id+"F0.wireOp",EDGE,"E0.bottom");var subQ3=sQuery(id+"F0.wireOp",EDGE,"E0.left");Q1=makeQuery(id+"F25.boolean.opBoolean","SPLIT",FACE,{"disambiguationData":[TD([makeQuery(id+"F2.opShell","OFFSET_FACE",FACE,{"disambiguationData":[OSD([subQ2])]})])],"derivedFrom":makeQuery(id+"F2.opShell","OFFSET_FACE",FACE,{"disambiguationData":[OSD([subQ3])]})});}
            extrude(context, id + "F30", {"entities" : qUnion([Q0]), "operationType" : NewBodyOperationType.REMOVE, "endBound" : BoundingType.UP_TO_SURFACE, "oppositeDirection" : true, "depth" : 25 * mm, "endBoundEntityFace" : qUnion([Q1]), "offsetDistance" : 25 * mm});
        }
        {
            var Q0;
            {var subQ1=sQuery(id+"F12.wireOp",EDGE,"E22.bottom");var subQ3=sQuery(id+"F0.wireOp",EDGE,"E0.bottom");var subQ4=sQuery(id+"F0.wireOp",EDGE,"E0.right");var subQ5=sQuery(id+"F0.wireOp",EDGE,"E0.top");var subQ9=sQuery(id+"F0.wireOp",EDGE,"E0.left");Q0=makeQuery(id+"F18.boolean.opBoolean","MERGE",FACE,{"derivedFrom":[makeQuery(id+"F16.boolean.opBoolean","SPLIT",FACE,{"disambiguationData":[TD([makeQuery(id+"F1.opExtrude","SWEPT_FACE",FACE,{"disambiguationData":[OSD([subQ3])]})])],"derivedFrom":makeQuery(id+"F13.boolean.opBoolean","MERGE",FACE,{"derivedFrom":[makeQuery(id+"F1.opExtrude","CAP_FACE",FACE,{"disambiguationData":[OSD([subQ3,subQ5,subQ9,subQ4])],"isStart":false}),makeQuery(id+"F13.opExtrude","SWEPT_FACE",FACE,{"disambiguationData":[OSD([subQ1])]})]})}),makeQuery(id+"F18.opExtrude","SWEPT_FACE",FACE,{"disambiguationData":[OSD([sQuery(id+"F17.wireOp",EDGE,"E35.bottom")])]})]});}
            var sketch = newSketch(context, id + "F31", { "sketchPlane" : qUnion([Q0])});
            skLineSegment(sketch, "E60.bottom", {"start": v(196, 0) * mm, "end": v(189, 0) * mm});
            skLineSegment(sketch, "E60.top", {"start": v(196, 94.5) * mm, "end": v(189, 94.5) * mm});
            skLineSegment(sketch, "E60.left", {"start": v(196, 0) * mm, "end": v(196, 94.5) * mm});
            skLineSegment(sketch, "E60.right", {"start": v(189, 0) * mm, "end": v(189, 94.5) * mm});
            skCircle(sketch, "E61", {"center": v(192.5, 5) * mm, "radius": 1.5 * mm});
            skCircle(sketch, "E62", {"center": v(192.5, 49) * mm, "radius": 1.5 * mm});
            skCircle(sketch, "E63", {"center": v(192.5, 89.5) * mm, "radius": 1.5 * mm});
            skSolve(sketch);
        }
        {
            var Q0;
            Q0=qSketchRegion(id+"F31",true);
            extrude(context, id + "F32", {"entities" : qUnion([Q0]), "operationType" : NewBodyOperationType.ADD, "depth" : 30 * mm, "offsetDistance" : 25 * mm});
        }
        {
            var Q0;
            Q0=makeQuery(id+"F1.opExtrude","SWEPT_FACE",FACE,{"disambiguationData":[OSD([sQuery(id+"F0.wireOp",EDGE,"E0.right")])]});
            var sketch = newSketch(context, id + "F33", { "sketchPlane" : qUnion([Q0])});
            skCircle(sketch, "E64", {"center": v(47.25, 39) * mm, "radius": 34 * mm});
            skCircle(sketch, "E65", {"center": v(16.5, 8.25) * mm, "radius": 1.75 * mm});
            skCircle(sketch, "E66", {"center": v(16.5, 69.75) * mm, "radius": 1.75 * mm});
            skCircle(sketch, "E67", {"center": v(78, 69.75) * mm, "radius": 1.75 * mm});
            skCircle(sketch, "E68", {"center": v(78, 8.25) * mm, "radius": 1.75 * mm});
            skSolve(sketch);
        }
        {
            var Q0;
            Q0=qSketchRegion(id+"F33",true);
            extrude(context, id + "F34", {"entities" : qUnion([Q0]), "operationType" : NewBodyOperationType.REMOVE, "oppositeDirection" : true, "depth" : 25 * mm, "offsetDistance" : 25 * mm});
        }
        {
            var Q0;
            {var subQ4=sQuery(id+"F12.wireOp",EDGE,"E22.bottom");var subQ10=sQuery(id+"F0.wireOp",EDGE,"E0.left");var subQ12=sQuery(id+"F0.wireOp",EDGE,"E0.top");var subQ13=makeQuery(id+"F1.opExtrude","SWEPT_FACE",FACE,{"disambiguationData":[OSD([subQ12])]});var subQ15=sQuery(id+"F17.wireOp",EDGE,"E35.bottom");var subQ20=sQuery(id+"F0.wireOp",EDGE,"E0.bottom");var subQ21=sQuery(id+"F0.wireOp",EDGE,"E0.right");Q0=makeQuery(id+"F32.boolean.opBoolean","SPLIT",FACE,{"disambiguationData":[TD([subQ13])],"derivedFrom":makeQuery(id+"F18.boolean.opBoolean","MERGE",FACE,{"derivedFrom":[makeQuery(id+"F16.boolean.opBoolean","SPLIT",FACE,{"disambiguationData":[TD([makeQuery(id+"F1.opExtrude","SWEPT_FACE",FACE,{"disambiguationData":[OSD([subQ20])]})])],"derivedFrom":makeQuery(id+"F13.boolean.opBoolean","MERGE",FACE,{"derivedFrom":[makeQuery(id+"F1.opExtrude","CAP_FACE",FACE,{"disambiguationData":[OSD([subQ20,subQ12,subQ10,subQ21])],"isStart":false}),makeQuery(id+"F13.opExtrude","SWEPT_FACE",FACE,{"disambiguationData":[OSD([subQ4])]})]})}),makeQuery(id+"F18.opExtrude","SWEPT_FACE",FACE,{"disambiguationData":[OSD([subQ15])]})]})});}
            var sketch = newSketch(context, id + "F35", { "sketchPlane" : qUnion([Q0])});
            skLineSegment(sketch, "E69.bottom", {"start": v(196.11, 0) * mm, "end": v(0, 0) * mm});
            skLineSegment(sketch, "E69.top", {"start": v(196.11, 94.5) * mm, "end": v(0, 94.5) * mm});
            skLineSegment(sketch, "E69.left", {"start": v(196.11, 0) * mm, "end": v(196.11, 94.5) * mm});
            skLineSegment(sketch, "E69.right", {"start": v(0, 0) * mm, "end": v(0, 94.5) * mm});
            skSolve(sketch);
        }
        {
            var Q0;
            Q0=makeQuery(id+"F1.opExtrude","SWEPT_EDGE",EDGE,{"disambiguationData":[OSD([sQuery(id+"F0.wireOp",EDGE,"E0.bottom"),sQuery(id+"F0.wireOp",EDGE,"E0.left")])]});
            var Q1;
            Q1=makeQuery(id+"F23.boolean.opBoolean","COPY",EDGE,{"derivedFrom":makeQuery(id+"F23.opExtrude","SWEPT_EDGE",EDGE,{"disambiguationData":[OSD([sQuery(id+"F0.wireOp",EDGE,"E0.left"),sQuery(id+"F22.wireOp",EDGE,"E42.top"),sQuery(id+"F22.wireOp",EDGE,"E42.left")])]})});
            var Q2;
            Q2=makeQuery(id+"F1.opExtrude","SWEPT_EDGE",EDGE,{"disambiguationData":[OSD([sQuery(id+"F0.wireOp",EDGE,"E0.top"),sQuery(id+"F0.wireOp",EDGE,"E0.right")])]});
            var Q3;
            Q3=makeQuery(id+"F1.opExtrude","SWEPT_EDGE",EDGE,{"disambiguationData":[OSD([sQuery(id+"F0.wireOp",EDGE,"E0.bottom"),sQuery(id+"F0.wireOp",EDGE,"E0.right")])]});
            var Q4;
            Q4=makeQuery(id+"F23.boolean.opBoolean","COPY",EDGE,{"derivedFrom":makeQuery(id+"F23.opExtrude","SWEPT_EDGE",EDGE,{"disambiguationData":[OSD([sQuery(id+"F0.wireOp",EDGE,"E0.top"),sQuery(id+"F22.wireOp",EDGE,"E42.bottom"),sQuery(id+"F22.wireOp",EDGE,"E42.right")])]})});
            fillet(context, id + "F36", {"entities" : qUnion([Q0, Q1, Q2, Q3, Q4]), "radius" : 3 * mm, "tangentPropagation" : true, "allowEdgeOverflow" : false});
        }
        {
            var Q0;
            Q0=qSketchRegion(id+"F35",true);
            extrude(context, id + "F37", {"entities" : qUnion([Q0]), "depth" : 55 * mm, "offsetDistance" : 25 * mm});
        }
        {
            var Q0;
            Q0=makeQuery(id+"F37.opExtrude","CAP_FACE",FACE,{"disambiguationData":[OSD([sQuery(id+"F35.wireOp",EDGE,"E69.bottom"),sQuery(id+"F35.wireOp",EDGE,"E69.top"),sQuery(id+"F35.wireOp",EDGE,"E69.left"),sQuery(id+"F35.wireOp",EDGE,"E69.right")])],"isStart":true});
            var sketch = newSketch(context, id + "F38", { "sketchPlane" : qUnion([Q0])});
            skLineSegment(sketch, "E70.bottom", {"start": v(189, -90.5) * mm, "end": v(7, -90.5) * mm});
            skLineSegment(sketch, "E70.top", {"start": v(189, -4) * mm, "end": v(7, -4) * mm});
            skLineSegment(sketch, "E70.left", {"start": v(189, -90.5) * mm, "end": v(189, -4) * mm});
            skLineSegment(sketch, "E70.right", {"start": v(7, -90.5) * mm, "end": v(7, -4) * mm});
            skSolve(sketch);
        }
        {
            var Q0;
            Q0=qSketchRegion(id+"F38",true);
            extrude(context, id + "F39", {"entities" : qUnion([Q0]), "operationType" : NewBodyOperationType.REMOVE, "oppositeDirection" : true, "depth" : 51 * mm, "offsetDistance" : 25 * mm});
        }
        {
            var Q0;
            Q0=makeQuery(id+"F37.opExtrude","CAP_FACE",FACE,{"disambiguationData":[OSD([sQuery(id+"F35.wireOp",EDGE,"E69.bottom"),sQuery(id+"F35.wireOp",EDGE,"E69.top"),sQuery(id+"F35.wireOp",EDGE,"E69.left"),sQuery(id+"F35.wireOp",EDGE,"E69.right")])],"isStart":true});
            var sketch = newSketch(context, id + "F40", { "sketchPlane" : qUnion([Q0])});
            skLineSegment(sketch, "E71.bottom", {"start": v(196.11, -94.5) * mm, "end": v(189, -94.5) * mm});
            skLineSegment(sketch, "E71.top", {"start": v(196.11, 0) * mm, "end": v(189, 0) * mm});
            skLineSegment(sketch, "E71.left", {"start": v(196.11, -94.5) * mm, "end": v(196.11, 0) * mm});
            skLineSegment(sketch, "E71.right", {"start": v(189, -94.5) * mm, "end": v(189, 0) * mm});
            skSolve(sketch);
        }
        {
            var Q0;
            Q0=qSketchRegion(id+"F40",true);
            extrude(context, id + "F41", {"entities" : qUnion([Q0]), "operationType" : NewBodyOperationType.REMOVE, "oppositeDirection" : true, "depth" : 30 * mm, "offsetDistance" : 25 * mm});
        }
        {
            var Q0;
            Q0=makeQuery(id+"F37.opExtrude","SWEPT_FACE",FACE,{"disambiguationData":[OSD([sQuery(id+"F35.wireOp",EDGE,"E69.right")])]});
            var sketch = newSketch(context, id + "F42", { "sketchPlane" : qUnion([Q0])});
            skCircle(sketch, "E72", {"center": v(-69.5, 77.5) * mm, "radius": 12.5 * mm});
            skCircle(sketch, "E73", {"center": v(-25, 77.5) * mm, "radius": 12.5 * mm});
            skCircle(sketch, "E74", {"center": v(-57, 65) * mm, "radius": 1.75 * mm});
            skCircle(sketch, "E75", {"center": v(-37.5, 90) * mm, "radius": 1.75 * mm});
            skCircle(sketch, "E76", {"center": v(-12.5, 90) * mm, "radius": 1.75 * mm});
            skCircle(sketch, "E77", {"center": v(-82, 90) * mm, "radius": 1.75 * mm});
            skCircle(sketch, "E78", {"center": v(-57, 90) * mm, "radius": 1.75 * mm});
            skCircle(sketch, "E79", {"center": v(-12.5, 65) * mm, "radius": 1.75 * mm});
            skCircle(sketch, "E80", {"center": v(-37.5, 65) * mm, "radius": 1.75 * mm});
            skCircle(sketch, "E81", {"center": v(-82, 65) * mm, "radius": 1.75 * mm});
            skArc(sketch, "E82", {"start": v(-85.62, 57.06) * mm, "mid": v(-85.06, 55.38) * mm, "end": v(-83.38, 55.94) * mm});
            skArc(sketch, "E83", {"start": v(-81.38, 59.94) * mm, "mid": v(-81.94, 61.62) * mm, "end": v(-83.62, 61.06) * mm});
            skLineSegment(sketch, "E84", {"start": v(-81.38, 59.94) * mm, "end": v(-83.38, 55.94) * mm});
            skLineSegment(sketch, "E85", {"start": v(-83.62, 61.06) * mm, "end": v(-85.62, 57.06) * mm});
            skArc(sketch, "E86.0.1.0", {"start": v(-85.6, 95.06) * mm, "mid": v(-85.04, 93.38) * mm, "end": v(-83.36, 93.94) * mm});
            skLineSegment(sketch, "E86.0.1.1", {"start": v(-83.6, 99.06) * mm, "end": v(-85.6, 95.06) * mm});
            skLineSegment(sketch, "E86.0.1.2", {"start": v(-81.36, 97.94) * mm, "end": v(-83.36, 93.94) * mm});
            skArc(sketch, "E86.0.1.3", {"start": v(-81.36, 97.94) * mm, "mid": v(-81.92, 99.62) * mm, "end": v(-83.6, 99.06) * mm});
            skArc(sketch, "E86.1.0.0", {"start": v(-77.62, 57.06) * mm, "mid": v(-77.06, 55.38) * mm, "end": v(-75.38, 55.94) * mm});
            skLineSegment(sketch, "E86.1.0.1", {"start": v(-75.62, 61.06) * mm, "end": v(-77.62, 57.06) * mm});
            skLineSegment(sketch, "E86.1.0.2", {"start": v(-73.38, 59.94) * mm, "end": v(-75.38, 55.94) * mm});
            skArc(sketch, "E86.1.0.3", {"start": v(-73.38, 59.94) * mm, "mid": v(-73.94, 61.62) * mm, "end": v(-75.62, 61.06) * mm});
            skArc(sketch, "E86.1.1.0", {"start": v(-77.6, 95.06) * mm, "mid": v(-77.04, 93.38) * mm, "end": v(-75.36, 93.94) * mm});
            skLineSegment(sketch, "E86.1.1.1", {"start": v(-75.6, 99.06) * mm, "end": v(-77.6, 95.06) * mm});
            skLineSegment(sketch, "E86.1.1.2", {"start": v(-73.36, 97.94) * mm, "end": v(-75.36, 93.94) * mm});
            skArc(sketch, "E86.1.1.3", {"start": v(-73.36, 97.94) * mm, "mid": v(-73.92, 99.62) * mm, "end": v(-75.6, 99.06) * mm});
            skArc(sketch, "E86.2.0.0", {"start": v(-69.62, 57.06) * mm, "mid": v(-69.06, 55.38) * mm, "end": v(-67.38, 55.94) * mm});
            skLineSegment(sketch, "E86.2.0.1", {"start": v(-67.62, 61.06) * mm, "end": v(-69.62, 57.06) * mm});
            skLineSegment(sketch, "E86.2.0.2", {"start": v(-65.38, 59.94) * mm, "end": v(-67.38, 55.94) * mm});
            skArc(sketch, "E86.2.0.3", {"start": v(-65.38, 59.94) * mm, "mid": v(-65.94, 61.62) * mm, "end": v(-67.62, 61.06) * mm});
            skArc(sketch, "E86.2.1.0", {"start": v(-69.6, 95.06) * mm, "mid": v(-69.04, 93.38) * mm, "end": v(-67.36, 93.94) * mm});
            skLineSegment(sketch, "E86.2.1.1", {"start": v(-67.6, 99.06) * mm, "end": v(-69.6, 95.06) * mm});
            skLineSegment(sketch, "E86.2.1.2", {"start": v(-65.36, 97.94) * mm, "end": v(-67.36, 93.94) * mm});
            skArc(sketch, "E86.2.1.3", {"start": v(-65.36, 97.94) * mm, "mid": v(-65.92, 99.62) * mm, "end": v(-67.6, 99.06) * mm});
            skArc(sketch, "E86.3.0.0", {"start": v(-61.62, 57.06) * mm, "mid": v(-61.06, 55.38) * mm, "end": v(-59.38, 55.94) * mm});
            skLineSegment(sketch, "E86.3.0.1", {"start": v(-59.62, 61.06) * mm, "end": v(-61.62, 57.06) * mm});
            skLineSegment(sketch, "E86.3.0.2", {"start": v(-57.38, 59.94) * mm, "end": v(-59.38, 55.94) * mm});
            skArc(sketch, "E86.3.0.3", {"start": v(-57.38, 59.94) * mm, "mid": v(-57.94, 61.62) * mm, "end": v(-59.62, 61.06) * mm});
            skArc(sketch, "E86.3.1.0", {"start": v(-61.6, 95.06) * mm, "mid": v(-61.04, 93.38) * mm, "end": v(-59.36, 93.94) * mm});
            skLineSegment(sketch, "E86.3.1.1", {"start": v(-59.6, 99.06) * mm, "end": v(-61.6, 95.06) * mm});
            skLineSegment(sketch, "E86.3.1.2", {"start": v(-57.36, 97.94) * mm, "end": v(-59.36, 93.94) * mm});
            skArc(sketch, "E86.3.1.3", {"start": v(-57.36, 97.94) * mm, "mid": v(-57.92, 99.62) * mm, "end": v(-59.6, 99.06) * mm});
            skArc(sketch, "E86.4.0.0", {"start": v(-53.62, 57.06) * mm, "mid": v(-53.06, 55.38) * mm, "end": v(-51.38, 55.94) * mm});
            skLineSegment(sketch, "E86.4.0.1", {"start": v(-51.62, 61.06) * mm, "end": v(-53.62, 57.06) * mm});
            skLineSegment(sketch, "E86.4.0.2", {"start": v(-49.38, 59.94) * mm, "end": v(-51.38, 55.94) * mm});
            skArc(sketch, "E86.4.0.3", {"start": v(-49.38, 59.94) * mm, "mid": v(-49.94, 61.62) * mm, "end": v(-51.62, 61.06) * mm});
            skArc(sketch, "E86.4.1.0", {"start": v(-53.6, 95.06) * mm, "mid": v(-53.04, 93.38) * mm, "end": v(-51.36, 93.94) * mm});
            skLineSegment(sketch, "E86.4.1.1", {"start": v(-51.6, 99.06) * mm, "end": v(-53.6, 95.06) * mm});
            skLineSegment(sketch, "E86.4.1.2", {"start": v(-49.36, 97.94) * mm, "end": v(-51.36, 93.94) * mm});
            skArc(sketch, "E86.4.1.3", {"start": v(-49.36, 97.94) * mm, "mid": v(-49.92, 99.62) * mm, "end": v(-51.6, 99.06) * mm});
            skArc(sketch, "E86.5.0.0", {"start": v(-45.62, 57.06) * mm, "mid": v(-45.06, 55.38) * mm, "end": v(-43.38, 55.94) * mm});
            skLineSegment(sketch, "E86.5.0.1", {"start": v(-43.62, 61.06) * mm, "end": v(-45.62, 57.06) * mm});
            skLineSegment(sketch, "E86.5.0.2", {"start": v(-41.38, 59.94) * mm, "end": v(-43.38, 55.94) * mm});
            skArc(sketch, "E86.5.0.3", {"start": v(-41.38, 59.94) * mm, "mid": v(-41.94, 61.62) * mm, "end": v(-43.62, 61.06) * mm});
            skArc(sketch, "E86.5.1.0", {"start": v(-45.6, 95.06) * mm, "mid": v(-45.04, 93.38) * mm, "end": v(-43.36, 93.94) * mm});
            skLineSegment(sketch, "E86.5.1.1", {"start": v(-43.6, 99.06) * mm, "end": v(-45.6, 95.06) * mm});
            skLineSegment(sketch, "E86.5.1.2", {"start": v(-41.36, 97.94) * mm, "end": v(-43.36, 93.94) * mm});
            skArc(sketch, "E86.5.1.3", {"start": v(-41.36, 97.94) * mm, "mid": v(-41.92, 99.62) * mm, "end": v(-43.6, 99.06) * mm});
            skArc(sketch, "E86.6.0.0", {"start": v(-37.62, 57.06) * mm, "mid": v(-37.06, 55.38) * mm, "end": v(-35.38, 55.94) * mm});
            skLineSegment(sketch, "E86.6.0.1", {"start": v(-35.62, 61.06) * mm, "end": v(-37.62, 57.06) * mm});
            skLineSegment(sketch, "E86.6.0.2", {"start": v(-33.38, 59.94) * mm, "end": v(-35.38, 55.94) * mm});
            skArc(sketch, "E86.6.0.3", {"start": v(-33.38, 59.94) * mm, "mid": v(-33.94, 61.62) * mm, "end": v(-35.62, 61.06) * mm});
            skArc(sketch, "E86.6.1.0", {"start": v(-37.6, 95.06) * mm, "mid": v(-37.04, 93.38) * mm, "end": v(-35.36, 93.94) * mm});
            skLineSegment(sketch, "E86.6.1.1", {"start": v(-35.6, 99.06) * mm, "end": v(-37.6, 95.06) * mm});
            skLineSegment(sketch, "E86.6.1.2", {"start": v(-33.36, 97.94) * mm, "end": v(-35.36, 93.94) * mm});
            skArc(sketch, "E86.6.1.3", {"start": v(-33.36, 97.94) * mm, "mid": v(-33.92, 99.62) * mm, "end": v(-35.6, 99.06) * mm});
            skArc(sketch, "E86.7.0.0", {"start": v(-29.62, 57.06) * mm, "mid": v(-29.06, 55.38) * mm, "end": v(-27.38, 55.94) * mm});
            skLineSegment(sketch, "E86.7.0.1", {"start": v(-27.62, 61.06) * mm, "end": v(-29.62, 57.06) * mm});
            skLineSegment(sketch, "E86.7.0.2", {"start": v(-25.38, 59.94) * mm, "end": v(-27.38, 55.94) * mm});
            skArc(sketch, "E86.7.0.3", {"start": v(-25.38, 59.94) * mm, "mid": v(-25.94, 61.62) * mm, "end": v(-27.62, 61.06) * mm});
            skArc(sketch, "E86.7.1.0", {"start": v(-29.6, 95.06) * mm, "mid": v(-29.04, 93.38) * mm, "end": v(-27.36, 93.94) * mm});
            skLineSegment(sketch, "E86.7.1.1", {"start": v(-27.6, 99.06) * mm, "end": v(-29.6, 95.06) * mm});
            skLineSegment(sketch, "E86.7.1.2", {"start": v(-25.36, 97.94) * mm, "end": v(-27.36, 93.94) * mm});
            skArc(sketch, "E86.7.1.3", {"start": v(-25.36, 97.94) * mm, "mid": v(-25.92, 99.62) * mm, "end": v(-27.6, 99.06) * mm});
            skArc(sketch, "E86.8.0.0", {"start": v(-21.62, 57.06) * mm, "mid": v(-21.06, 55.38) * mm, "end": v(-19.38, 55.94) * mm});
            skLineSegment(sketch, "E86.8.0.1", {"start": v(-19.62, 61.06) * mm, "end": v(-21.62, 57.06) * mm});
            skLineSegment(sketch, "E86.8.0.2", {"start": v(-17.38, 59.94) * mm, "end": v(-19.38, 55.94) * mm});
            skArc(sketch, "E86.8.0.3", {"start": v(-17.38, 59.94) * mm, "mid": v(-17.94, 61.62) * mm, "end": v(-19.62, 61.06) * mm});
            skArc(sketch, "E86.8.1.0", {"start": v(-21.6, 95.06) * mm, "mid": v(-21.04, 93.38) * mm, "end": v(-19.36, 93.94) * mm});
            skLineSegment(sketch, "E86.8.1.1", {"start": v(-19.6, 99.06) * mm, "end": v(-21.6, 95.06) * mm});
            skLineSegment(sketch, "E86.8.1.2", {"start": v(-17.36, 97.94) * mm, "end": v(-19.36, 93.94) * mm});
            skArc(sketch, "E86.8.1.3", {"start": v(-17.36, 97.94) * mm, "mid": v(-17.92, 99.62) * mm, "end": v(-19.6, 99.06) * mm});
            skArc(sketch, "E86.9.0.0", {"start": v(-13.62, 57.06) * mm, "mid": v(-13.06, 55.38) * mm, "end": v(-11.38, 55.94) * mm});
            skLineSegment(sketch, "E86.9.0.1", {"start": v(-11.62, 61.06) * mm, "end": v(-13.62, 57.06) * mm});
            skLineSegment(sketch, "E86.9.0.2", {"start": v(-9.38, 59.94) * mm, "end": v(-11.38, 55.94) * mm});
            skArc(sketch, "E86.9.0.3", {"start": v(-9.38, 59.94) * mm, "mid": v(-9.94, 61.62) * mm, "end": v(-11.62, 61.06) * mm});
            skArc(sketch, "E86.9.1.0", {"start": v(-13.6, 95.06) * mm, "mid": v(-13.04, 93.38) * mm, "end": v(-11.36, 93.94) * mm});
            skLineSegment(sketch, "E86.9.1.1", {"start": v(-11.6, 99.06) * mm, "end": v(-13.6, 95.06) * mm});
            skLineSegment(sketch, "E86.9.1.2", {"start": v(-9.36, 97.94) * mm, "end": v(-11.36, 93.94) * mm});
            skArc(sketch, "E86.9.1.3", {"start": v(-9.36, 97.94) * mm, "mid": v(-9.92, 99.62) * mm, "end": v(-11.6, 99.06) * mm});
            skLineSegment(sketch, "E86.direction1", {"start": v(-85.62, 57.06) * mm, "end": v(-77.62, 57.06) * mm, "construction": true});
            skLineSegment(sketch, "E86.direction2", {"start": v(-85.62, 57.06) * mm, "end": v(-85.6, 95.06) * mm, "construction": true});
            skSolve(sketch);
        }
        {
            var Q0;
            Q0=qSketchRegion(id+"F42",true);
            extrude(context, id + "F43", {"entities" : qUnion([Q0]), "operationType" : NewBodyOperationType.REMOVE, "oppositeDirection" : true, "depth" : 25 * mm, "offsetDistance" : 25 * mm});
        }
        {
            var Q0;
            Q0=makeQuery(id+"F37.opExtrude","CAP_FACE",FACE,{"disambiguationData":[OSD([sQuery(id+"F35.wireOp",EDGE,"E69.bottom"),sQuery(id+"F35.wireOp",EDGE,"E69.top"),sQuery(id+"F35.wireOp",EDGE,"E69.left"),sQuery(id+"F35.wireOp",EDGE,"E69.right")])],"isStart":false});
            var sketch = newSketch(context, id + "F44", { "sketchPlane" : qUnion([Q0])});
            skCircle(sketch, "E87", {"center": v(168.11, 21) * mm, "radius": 12.5 * mm});
            skCircle(sketch, "E88", {"center": v(155.61, 33.5) * mm, "radius": 1.75 * mm});
            skCircle(sketch, "E89", {"center": v(180.61, 33.5) * mm, "radius": 1.75 * mm});
            skCircle(sketch, "E90", {"center": v(180.61, 8.5) * mm, "radius": 1.75 * mm});
            skCircle(sketch, "E91", {"center": v(155.61, 8.5) * mm, "radius": 1.75 * mm});
            skCircle(sketch, "E92.0.1.0", {"center": v(180.61, 43.5) * mm, "radius": 1.75 * mm});
            skCircle(sketch, "E92.0.1.1", {"center": v(180.61, 68.5) * mm, "radius": 1.75 * mm});
            skCircle(sketch, "E92.0.1.2", {"center": v(168.11, 56) * mm, "radius": 12.5 * mm});
            skCircle(sketch, "E92.0.1.3", {"center": v(155.61, 68.5) * mm, "radius": 1.75 * mm});
            skCircle(sketch, "E92.0.1.4", {"center": v(155.61, 43.5) * mm, "radius": 1.75 * mm});
            skCircle(sketch, "E92.1.0.0", {"center": v(140.61, 8.5) * mm, "radius": 1.75 * mm});
            skCircle(sketch, "E92.1.0.1", {"center": v(140.61, 33.5) * mm, "radius": 1.75 * mm});
            skCircle(sketch, "E92.1.0.2", {"center": v(128.11, 21) * mm, "radius": 12.5 * mm});
            skCircle(sketch, "E92.1.0.3", {"center": v(115.61, 33.5) * mm, "radius": 1.75 * mm});
            skCircle(sketch, "E92.1.0.4", {"center": v(115.61, 8.5) * mm, "radius": 1.75 * mm});
            skCircle(sketch, "E92.1.1.0", {"center": v(140.61, 43.5) * mm, "radius": 1.75 * mm});
            skCircle(sketch, "E92.1.1.1", {"center": v(140.61, 68.5) * mm, "radius": 1.75 * mm});
            skCircle(sketch, "E92.1.1.2", {"center": v(128.11, 56) * mm, "radius": 12.5 * mm});
            skCircle(sketch, "E92.1.1.3", {"center": v(115.61, 68.5) * mm, "radius": 1.75 * mm});
            skCircle(sketch, "E92.1.1.4", {"center": v(115.61, 43.5) * mm, "radius": 1.75 * mm});
            skLineSegment(sketch, "E92.direction1", {"start": v(155.61, 8.5) * mm, "end": v(115.61, 8.5) * mm, "construction": true});
            skLineSegment(sketch, "E92.direction2", {"start": v(155.61, 8.5) * mm, "end": v(155.61, 43.5) * mm, "construction": true});
            skCircle(sketch, "E93.1.0.0", {"center": v(45.61, 43.5) * mm, "radius": 1.75 * mm});
            skCircle(sketch, "E93.1.0.1", {"center": v(20.61, 8.5) * mm, "radius": 1.75 * mm});
            skLineSegment(sketch, "E93.1.0.2", {"start": v(60.61, 8.5) * mm, "end": v(60.61, 43.5) * mm, "construction": true});
            skCircle(sketch, "E93.1.0.3", {"center": v(20.61, 33.5) * mm, "radius": 1.75 * mm});
            skCircle(sketch, "E93.1.0.4", {"center": v(45.61, 33.5) * mm, "radius": 1.75 * mm});
            skCircle(sketch, "E93.1.0.5", {"center": v(20.61, 43.5) * mm, "radius": 1.75 * mm});
            skCircle(sketch, "E93.1.0.6", {"center": v(60.61, 43.5) * mm, "radius": 1.75 * mm});
            skCircle(sketch, "E93.1.0.7", {"center": v(60.61, 33.5) * mm, "radius": 1.75 * mm});
            skCircle(sketch, "E93.1.0.8", {"center": v(85.61, 33.5) * mm, "radius": 1.75 * mm});
            skCircle(sketch, "E93.1.0.9", {"center": v(33.11, 56) * mm, "radius": 12.5 * mm});
            skCircle(sketch, "E93.1.0.10", {"center": v(73.11, 56) * mm, "radius": 12.5 * mm});
            skCircle(sketch, "E93.1.0.11", {"center": v(20.61, 68.5) * mm, "radius": 1.75 * mm});
            skCircle(sketch, "E93.1.0.12", {"center": v(45.61, 68.5) * mm, "radius": 1.75 * mm});
            skCircle(sketch, "E93.1.0.13", {"center": v(73.11, 21) * mm, "radius": 12.5 * mm});
            skCircle(sketch, "E93.1.0.14", {"center": v(33.11, 21) * mm, "radius": 12.5 * mm});
            skCircle(sketch, "E93.1.0.15", {"center": v(45.61, 8.5) * mm, "radius": 1.75 * mm});
            skCircle(sketch, "E93.1.0.16", {"center": v(60.61, 68.5) * mm, "radius": 1.75 * mm});
            skCircle(sketch, "E93.1.0.17", {"center": v(60.61, 8.5) * mm, "radius": 1.75 * mm});
            skCircle(sketch, "E93.1.0.18", {"center": v(85.61, 8.5) * mm, "radius": 1.75 * mm});
            skCircle(sketch, "E93.1.0.19", {"center": v(85.61, 68.5) * mm, "radius": 1.75 * mm});
            skCircle(sketch, "E93.1.0.20", {"center": v(85.61, 43.5) * mm, "radius": 1.75 * mm});
            skLineSegment(sketch, "E93.direction1", {"start": v(115.61, 8.5) * mm, "end": v(20.61, 8.5) * mm, "construction": true});
            skCircle(sketch, "E94", {"center": v(3.5, 89.5) * mm, "radius": 1.5 * mm});
            skCircle(sketch, "E95", {"center": v(3.5, 49) * mm, "radius": 1.5 * mm});
            skCircle(sketch, "E96", {"center": v(3.5, 5) * mm, "radius": 1.5 * mm});
            skCircle(sketch, "E97", {"center": v(192.5, 89.5) * mm, "radius": 1.5 * mm});
            skCircle(sketch, "E98", {"center": v(192.5, 5) * mm, "radius": 1.5 * mm});
            skCircle(sketch, "E99", {"center": v(192.5, 49) * mm, "radius": 1.5 * mm});
            skLineSegment(sketch, "E100.bottom", {"start": v(0, 94.5) * mm, "end": v(10, 94.5) * mm});
            skLineSegment(sketch, "E100.top", {"start": v(0, 93.5) * mm, "end": v(10, 93.5) * mm});
            skLineSegment(sketch, "E100.left", {"start": v(0, 94.5) * mm, "end": v(0, 93.5) * mm});
            skLineSegment(sketch, "E100.right", {"start": v(10, 94.5) * mm, "end": v(10, 93.5) * mm});
            skSolve(sketch);
        }
        {
            var Q0;
            Q0=qSketchRegion(id+"F44",true);
            extrude(context, id + "F45", {"entities" : qUnion([Q0]), "operationType" : NewBodyOperationType.REMOVE, "endBound" : BoundingType.THROUGH_ALL, "oppositeDirection" : true, "depth" : 25 * mm, "offsetDistance" : 25 * mm});
        }
        {
            var Q0;
            Q0=makeQuery(id+"F37.opExtrude","CAP_FACE",FACE,{"disambiguationData":[OSD([sQuery(id+"F35.wireOp",EDGE,"E69.bottom"),sQuery(id+"F35.wireOp",EDGE,"E69.top"),sQuery(id+"F35.wireOp",EDGE,"E69.left"),sQuery(id+"F35.wireOp",EDGE,"E69.right")])],"isStart":false});
            var sketch = newSketch(context, id + "F46", { "sketchPlane" : qUnion([Q0])});
            skCircle(sketch, "E101", {"center": v(3.5, 89.5) * mm, "radius": 2.25 * mm});
            skCircle(sketch, "E102", {"center": v(3.5, 49) * mm, "radius": 2.25 * mm});
            skCircle(sketch, "E103", {"center": v(3.5, 5) * mm, "radius": 2.25 * mm});
            skCircle(sketch, "E104", {"center": v(192.5, 89.5) * mm, "radius": 2.25 * mm});
            skCircle(sketch, "E105", {"center": v(192.5, 49) * mm, "radius": 2.25 * mm});
            skCircle(sketch, "E106", {"center": v(192.5, 5) * mm, "radius": 2.25 * mm});
            skSolve(sketch);
        }
        {
            var Q0;
            Q0=makeQuery(id+"F46.imprint","IMPRINT",FACE,{"disambiguationData":[TD([[makeQuery(id+"F46.imprint","IMPRINT",EDGE,{"derivedFrom":sQuery(id+"F46.wireOp",EDGE,"E101")}),1.0]])]});
            var Q1;
            Q1=makeQuery(id+"F46.imprint","IMPRINT",FACE,{"disambiguationData":[TD([[makeQuery(id+"F46.imprint","IMPRINT",EDGE,{"derivedFrom":sQuery(id+"F46.wireOp",EDGE,"E102")}),1.0]])]});
            var Q2;
            Q2=makeQuery(id+"F46.imprint","IMPRINT",FACE,{"disambiguationData":[TD([[makeQuery(id+"F46.imprint","IMPRINT",EDGE,{"derivedFrom":sQuery(id+"F46.wireOp",EDGE,"E103")}),1.0]])]});
            var Q3;
            Q3=makeQuery(id+"F37.opExtrude","CAP_FACE",FACE,{"disambiguationData":[OSD([sQuery(id+"F35.wireOp",EDGE,"E69.bottom"),sQuery(id+"F35.wireOp",EDGE,"E69.top"),sQuery(id+"F35.wireOp",EDGE,"E69.left"),sQuery(id+"F35.wireOp",EDGE,"E69.right")])],"isStart":true});
            extrude(context, id + "F47", {"entities" : qUnion([Q0, Q1, Q2]), "operationType" : NewBodyOperationType.REMOVE, "endBound" : BoundingType.UP_TO_SURFACE, "oppositeDirection" : true, "depth" : 25 * mm, "endBoundEntityFace" : qUnion([Q3]), "hasOffset" : true, "offsetDistance" : 10 * mm});
        }
        {
            var Q0;
            Q0=makeQuery(id+"F46.imprint","IMPRINT",FACE,{"disambiguationData":[TD([[makeQuery(id+"F46.imprint","IMPRINT",EDGE,{"derivedFrom":makeQuery(id+"F45.boolean.opBoolean","COPY",EDGE,{"derivedFrom":makeQuery(id+"F45.opExtrude","CAP_EDGE",EDGE,{"disambiguationData":[OSD([sQuery(id+"F44.wireOp",EDGE,"E97")])],"isStart":true})})}),1.0]])]});
            var Q1;
            Q1=makeQuery(id+"F46.imprint","IMPRINT",FACE,{"disambiguationData":[TD([[makeQuery(id+"F46.imprint","IMPRINT",EDGE,{"derivedFrom":sQuery(id+"F46.wireOp",EDGE,"E104")}),1.0]])]});
            var Q2;
            Q2=makeQuery(id+"F46.imprint","IMPRINT",FACE,{"disambiguationData":[TD([[makeQuery(id+"F46.imprint","IMPRINT",EDGE,{"derivedFrom":sQuery(id+"F46.wireOp",EDGE,"E105")}),1.0]])]});
            var Q3;
            Q3=makeQuery(id+"F46.imprint","IMPRINT",FACE,{"disambiguationData":[TD([[makeQuery(id+"F46.imprint","IMPRINT",EDGE,{"derivedFrom":sQuery(id+"F46.wireOp",EDGE,"E106")}),1.0]])]});
            var Q4;
            Q4=makeQuery(id+"F41.boolean.opBoolean","COPY",FACE,{"derivedFrom":makeQuery(id+"F41.opExtrude","CAP_FACE",FACE,{"disambiguationData":[OSD([sQuery(id+"F40.wireOp",EDGE,"E71.bottom"),sQuery(id+"F40.wireOp",EDGE,"E71.top"),sQuery(id+"F40.wireOp",EDGE,"E71.left"),sQuery(id+"F40.wireOp",EDGE,"E71.right")])],"isStart":false})});
            extrude(context, id + "F48", {"entities" : qUnion([Q0, Q1, Q2, Q3]), "operationType" : NewBodyOperationType.REMOVE, "endBound" : BoundingType.UP_TO_SURFACE, "oppositeDirection" : true, "depth" : 25 * mm, "endBoundEntityFace" : qUnion([Q4]), "hasOffset" : true, "offsetDistance" : 10 * mm});
        }
        {
            var Q0;
            Q0=makeQuery(id+"F39.boolean.opBoolean","COPY",FACE,{"derivedFrom":makeQuery(id+"F39.opExtrude","SWEPT_FACE",FACE,{"disambiguationData":[OSD([sQuery(id+"F38.wireOp",EDGE,"E70.bottom")])]})});
            var sketch = newSketch(context, id + "F49", { "sketchPlane" : qUnion([Q0])});
            skLineSegment(sketch, "E107.bottom", {"start": v(106.11, 64.5) * mm, "end": v(91.11, 64.5) * mm});
            skLineSegment(sketch, "E107.top", {"start": v(106.11, 34.5) * mm, "end": v(91.11, 34.5) * mm});
            skLineSegment(sketch, "E107.left", {"start": v(106.11, 64.5) * mm, "end": v(106.11, 34.5) * mm});
            skLineSegment(sketch, "E107.right", {"start": v(91.11, 64.5) * mm, "end": v(91.11, 34.5) * mm});
            skSolve(sketch);
        }
        {
            var Q0;
            Q0=qSketchRegion(id+"F49",true);
            extrude(context, id + "F50", {"entities" : qUnion([Q0]), "operationType" : NewBodyOperationType.ADD, "depth" : 12 * mm, "offsetDistance" : 25 * mm});
        }
        {
            var Q0;
            Q0=makeQuery(id+"F39.boolean.opBoolean","COPY",FACE,{"derivedFrom":makeQuery(id+"F39.opExtrude","SWEPT_FACE",FACE,{"disambiguationData":[OSD([sQuery(id+"F38.wireOp",EDGE,"E70.top")])]})});
            var sketch = newSketch(context, id + "F51", { "sketchPlane" : qUnion([Q0])});
            skLineSegment(sketch, "E108.bottom", {"start": v(-106.11, 64.5) * mm, "end": v(-91.11, 64.5) * mm});
            skLineSegment(sketch, "E108.top", {"start": v(-106.11, 34.5) * mm, "end": v(-91.11, 34.5) * mm});
            skLineSegment(sketch, "E108.left", {"start": v(-106.11, 64.5) * mm, "end": v(-106.11, 34.5) * mm});
            skLineSegment(sketch, "E108.right", {"start": v(-91.11, 64.5) * mm, "end": v(-91.11, 34.5) * mm});
            skSolve(sketch);
        }
        {
            var Q0;
            {var subQ0=sQuery(id+"F51.wireOp",EDGE,"E108.top");Q0=makeQuery(id+"F51.imprint","IMPRINT",FACE,{"disambiguationData":[TD([[makeQuery(id+"F51.imprint","IMPRINT",EDGE,{"derivedFrom":subQ0}),1.0]])]});}
            var Q1;
            {var subQ0=sQuery(id+"F51.wireOp",EDGE,"E108.bottom");Q1=makeQuery(id+"F51.imprint","IMPRINT",FACE,{"disambiguationData":[TD([[makeQuery(id+"F51.imprint","IMPRINT",EDGE,{"derivedFrom":subQ0}),-1.0]])]});}
            extrude(context, id + "F52", {"entities" : qUnion([Q0, Q1]), "operationType" : NewBodyOperationType.ADD, "depth" : 12 * mm, "offsetDistance" : 25 * mm});
        }
        {
            var Q0;
            Q0=makeQuery(id+"F37.opExtrude","SWEPT_FACE",FACE,{"disambiguationData":[OSD([sQuery(id+"F35.wireOp",EDGE,"E69.top")])]});
            var sketch = newSketch(context, id + "F53", { "sketchPlane" : qUnion([Q0])});
            skCircle(sketch, "E109", {"center": v(-96.11, 77.5) * mm, "radius": 12.5 * mm});
            skArc(sketch, "E110", {"start": v(-18.88, 95.94) * mm, "mid": v(-19.44, 97.62) * mm, "end": v(-21.12, 97.06) * mm});
            skArc(sketch, "E111", {"start": v(-23.12, 93.06) * mm, "mid": v(-22.56, 91.38) * mm, "end": v(-20.88, 91.94) * mm});
            skLineSegment(sketch, "E112", {"start": v(-23.12, 93.06) * mm, "end": v(-21.12, 97.06) * mm});
            skLineSegment(sketch, "E113", {"start": v(-20.88, 91.94) * mm, "end": v(-18.88, 95.94) * mm});
            skLineSegment(sketch, "E114.0.1.0", {"start": v(-20.88, 81.94) * mm, "end": v(-18.88, 85.94) * mm});
            skArc(sketch, "E114.0.1.1", {"start": v(-23.12, 83.06) * mm, "mid": v(-22.56, 81.38) * mm, "end": v(-20.88, 81.94) * mm});
            skLineSegment(sketch, "E114.0.1.2", {"start": v(-23.12, 83.06) * mm, "end": v(-21.12, 87.06) * mm});
            skArc(sketch, "E114.0.1.3", {"start": v(-18.88, 85.94) * mm, "mid": v(-19.44, 87.62) * mm, "end": v(-21.12, 87.06) * mm});
            skLineSegment(sketch, "E114.1.0.0", {"start": v(-28.88, 91.94) * mm, "end": v(-26.88, 95.94) * mm});
            skArc(sketch, "E114.1.0.1", {"start": v(-31.12, 93.06) * mm, "mid": v(-30.56, 91.38) * mm, "end": v(-28.88, 91.94) * mm});
            skLineSegment(sketch, "E114.1.0.2", {"start": v(-31.12, 93.06) * mm, "end": v(-29.12, 97.06) * mm});
            skArc(sketch, "E114.1.0.3", {"start": v(-26.88, 95.94) * mm, "mid": v(-27.44, 97.62) * mm, "end": v(-29.12, 97.06) * mm});
            skLineSegment(sketch, "E114.1.1.0", {"start": v(-28.88, 81.94) * mm, "end": v(-26.88, 85.94) * mm});
            skArc(sketch, "E114.1.1.1", {"start": v(-31.12, 83.06) * mm, "mid": v(-30.56, 81.38) * mm, "end": v(-28.88, 81.94) * mm});
            skLineSegment(sketch, "E114.1.1.2", {"start": v(-31.12, 83.06) * mm, "end": v(-29.12, 87.06) * mm});
            skArc(sketch, "E114.1.1.3", {"start": v(-26.88, 85.94) * mm, "mid": v(-27.44, 87.62) * mm, "end": v(-29.12, 87.06) * mm});
            skLineSegment(sketch, "E114.2.0.0", {"start": v(-36.88, 91.94) * mm, "end": v(-34.88, 95.94) * mm});
            skArc(sketch, "E114.2.0.1", {"start": v(-39.12, 93.06) * mm, "mid": v(-38.56, 91.38) * mm, "end": v(-36.88, 91.94) * mm});
            skLineSegment(sketch, "E114.2.0.2", {"start": v(-39.12, 93.06) * mm, "end": v(-37.12, 97.06) * mm});
            skArc(sketch, "E114.2.0.3", {"start": v(-34.88, 95.94) * mm, "mid": v(-35.44, 97.62) * mm, "end": v(-37.12, 97.06) * mm});
            skLineSegment(sketch, "E114.2.1.0", {"start": v(-36.88, 81.94) * mm, "end": v(-34.88, 85.94) * mm});
            skArc(sketch, "E114.2.1.1", {"start": v(-39.12, 83.06) * mm, "mid": v(-38.56, 81.38) * mm, "end": v(-36.88, 81.94) * mm});
            skLineSegment(sketch, "E114.2.1.2", {"start": v(-39.12, 83.06) * mm, "end": v(-37.12, 87.06) * mm});
            skArc(sketch, "E114.2.1.3", {"start": v(-34.88, 85.94) * mm, "mid": v(-35.44, 87.62) * mm, "end": v(-37.12, 87.06) * mm});
            skLineSegment(sketch, "E114.3.0.0", {"start": v(-44.88, 91.94) * mm, "end": v(-42.88, 95.94) * mm});
            skArc(sketch, "E114.3.0.1", {"start": v(-47.12, 93.06) * mm, "mid": v(-46.56, 91.38) * mm, "end": v(-44.88, 91.94) * mm});
            skLineSegment(sketch, "E114.3.0.2", {"start": v(-47.12, 93.06) * mm, "end": v(-45.12, 97.06) * mm});
            skArc(sketch, "E114.3.0.3", {"start": v(-42.88, 95.94) * mm, "mid": v(-43.44, 97.62) * mm, "end": v(-45.12, 97.06) * mm});
            skLineSegment(sketch, "E114.3.1.0", {"start": v(-44.88, 81.94) * mm, "end": v(-42.88, 85.94) * mm});
            skArc(sketch, "E114.3.1.1", {"start": v(-47.12, 83.06) * mm, "mid": v(-46.56, 81.38) * mm, "end": v(-44.88, 81.94) * mm});
            skLineSegment(sketch, "E114.3.1.2", {"start": v(-47.12, 83.06) * mm, "end": v(-45.12, 87.06) * mm});
            skArc(sketch, "E114.3.1.3", {"start": v(-42.88, 85.94) * mm, "mid": v(-43.44, 87.62) * mm, "end": v(-45.12, 87.06) * mm});
            skLineSegment(sketch, "E114.4.0.0", {"start": v(-52.88, 91.94) * mm, "end": v(-50.88, 95.94) * mm});
            skArc(sketch, "E114.4.0.1", {"start": v(-55.12, 93.06) * mm, "mid": v(-54.56, 91.38) * mm, "end": v(-52.88, 91.94) * mm});
            skLineSegment(sketch, "E114.4.0.2", {"start": v(-55.12, 93.06) * mm, "end": v(-53.12, 97.06) * mm});
            skArc(sketch, "E114.4.0.3", {"start": v(-50.88, 95.94) * mm, "mid": v(-51.44, 97.62) * mm, "end": v(-53.12, 97.06) * mm});
            skLineSegment(sketch, "E114.4.1.0", {"start": v(-52.88, 81.94) * mm, "end": v(-50.88, 85.94) * mm});
            skArc(sketch, "E114.4.1.1", {"start": v(-55.12, 83.06) * mm, "mid": v(-54.56, 81.38) * mm, "end": v(-52.88, 81.94) * mm});
            skLineSegment(sketch, "E114.4.1.2", {"start": v(-55.12, 83.06) * mm, "end": v(-53.12, 87.06) * mm});
            skArc(sketch, "E114.4.1.3", {"start": v(-50.88, 85.94) * mm, "mid": v(-51.44, 87.62) * mm, "end": v(-53.12, 87.06) * mm});
            skLineSegment(sketch, "E114.5.0.0", {"start": v(-60.88, 91.94) * mm, "end": v(-58.88, 95.94) * mm});
            skArc(sketch, "E114.5.0.1", {"start": v(-63.12, 93.06) * mm, "mid": v(-62.56, 91.38) * mm, "end": v(-60.88, 91.94) * mm});
            skLineSegment(sketch, "E114.5.0.2", {"start": v(-63.12, 93.06) * mm, "end": v(-61.12, 97.06) * mm});
            skArc(sketch, "E114.5.0.3", {"start": v(-58.88, 95.94) * mm, "mid": v(-59.44, 97.62) * mm, "end": v(-61.12, 97.06) * mm});
            skLineSegment(sketch, "E114.5.1.0", {"start": v(-60.88, 81.94) * mm, "end": v(-58.88, 85.94) * mm});
            skArc(sketch, "E114.5.1.1", {"start": v(-63.12, 83.06) * mm, "mid": v(-62.56, 81.38) * mm, "end": v(-60.88, 81.94) * mm});
            skLineSegment(sketch, "E114.5.1.2", {"start": v(-63.12, 83.06) * mm, "end": v(-61.12, 87.06) * mm});
            skArc(sketch, "E114.5.1.3", {"start": v(-58.88, 85.94) * mm, "mid": v(-59.44, 87.62) * mm, "end": v(-61.12, 87.06) * mm});
            skLineSegment(sketch, "E114.6.0.0", {"start": v(-68.88, 91.94) * mm, "end": v(-66.88, 95.94) * mm});
            skArc(sketch, "E114.6.0.1", {"start": v(-71.12, 93.06) * mm, "mid": v(-70.56, 91.38) * mm, "end": v(-68.88, 91.94) * mm});
            skLineSegment(sketch, "E114.6.0.2", {"start": v(-71.12, 93.06) * mm, "end": v(-69.12, 97.06) * mm});
            skArc(sketch, "E114.6.0.3", {"start": v(-66.88, 95.94) * mm, "mid": v(-67.44, 97.62) * mm, "end": v(-69.12, 97.06) * mm});
            skLineSegment(sketch, "E114.6.1.0", {"start": v(-68.88, 81.94) * mm, "end": v(-66.88, 85.94) * mm});
            skArc(sketch, "E114.6.1.1", {"start": v(-71.12, 83.06) * mm, "mid": v(-70.56, 81.38) * mm, "end": v(-68.88, 81.94) * mm});
            skLineSegment(sketch, "E114.6.1.2", {"start": v(-71.12, 83.06) * mm, "end": v(-69.12, 87.06) * mm});
            skArc(sketch, "E114.6.1.3", {"start": v(-66.88, 85.94) * mm, "mid": v(-67.44, 87.62) * mm, "end": v(-69.12, 87.06) * mm});
            skLineSegment(sketch, "E114.7.0.0", {"start": v(-76.88, 91.94) * mm, "end": v(-74.88, 95.94) * mm});
            skArc(sketch, "E114.7.0.1", {"start": v(-79.12, 93.06) * mm, "mid": v(-78.56, 91.38) * mm, "end": v(-76.88, 91.94) * mm});
            skLineSegment(sketch, "E114.7.0.2", {"start": v(-79.12, 93.06) * mm, "end": v(-77.12, 97.06) * mm});
            skArc(sketch, "E114.7.0.3", {"start": v(-74.88, 95.94) * mm, "mid": v(-75.44, 97.62) * mm, "end": v(-77.12, 97.06) * mm});
            skLineSegment(sketch, "E114.7.1.0", {"start": v(-76.88, 81.94) * mm, "end": v(-74.88, 85.94) * mm});
            skArc(sketch, "E114.7.1.1", {"start": v(-79.12, 83.06) * mm, "mid": v(-78.56, 81.38) * mm, "end": v(-76.88, 81.94) * mm});
            skLineSegment(sketch, "E114.7.1.2", {"start": v(-79.12, 83.06) * mm, "end": v(-77.12, 87.06) * mm});
            skArc(sketch, "E114.7.1.3", {"start": v(-74.88, 85.94) * mm, "mid": v(-75.44, 87.62) * mm, "end": v(-77.12, 87.06) * mm});
            skLineSegment(sketch, "E114.direction1", {"start": v(-23.12, 93.06) * mm, "end": v(-31.12, 93.06) * mm, "construction": true});
            skLineSegment(sketch, "E114.direction2", {"start": v(-23.12, 93.06) * mm, "end": v(-23.12, 83.06) * mm, "construction": true});
            skSolve(sketch);
        }
        {
            var Q0;
            Q0=qSketchRegion(id+"F53",true);
            extrude(context, id + "F54", {"entities" : qUnion([Q0]), "operationType" : NewBodyOperationType.REMOVE, "oppositeDirection" : true, "depth" : 25 * mm, "offsetDistance" : 25 * mm});
        }
        {
            var Q0;
            Q0=makeQuery(id+"F52.opExtrude","CAP_EDGE",EDGE,{"disambiguationData":[OSD([sQuery(id+"F51.wireOp",EDGE,"E108.bottom")])],"isStart":false});
            chamfer(context, id + "F55", {"entities" : qUnion([Q0]), "chamferType" : ChamferType.TWO_OFFSETS, "width1" : 12 * mm, "oppositeDirection" : false, "width2" : 20 * mm, "tangentPropagation" : true});
        }
        {
            var Q0;
            Q0=makeQuery(id+"F50.opExtrude","CAP_EDGE",EDGE,{"disambiguationData":[OSD([sQuery(id+"F49.wireOp",EDGE,"E107.bottom")])],"isStart":false});
            chamfer(context, id + "F56", {"entities" : qUnion([Q0]), "chamferType" : ChamferType.TWO_OFFSETS, "width1" : 20 * mm, "oppositeDirection" : false, "width2" : 12 * mm, "tangentPropagation" : true});
        }
        {
            var Q0;
            Q0=makeQuery(id+"F37.opExtrude","SWEPT_EDGE",EDGE,{"disambiguationData":[OSD([sQuery(id+"F35.wireOp",EDGE,"E69.bottom"),sQuery(id+"F35.wireOp",EDGE,"E69.right")])]});
            var Q1;
            Q1=makeQuery(id+"F45.boolean.opBoolean","COPY",EDGE,{"derivedFrom":makeQuery(id+"F45.opExtrude","SWEPT_EDGE",EDGE,{"disambiguationData":[OSD([sQuery(id+"F35.wireOp",EDGE,"E69.right"),sQuery(id+"F44.wireOp",EDGE,"E100.top"),sQuery(id+"F44.wireOp",EDGE,"E100.left")])]})});
            var Q2;
            Q2=makeQuery(id+"F37.opExtrude","SWEPT_EDGE",EDGE,{"disambiguationData":[OSD([sQuery(id+"F35.wireOp",EDGE,"E69.bottom"),sQuery(id+"F35.wireOp",EDGE,"E69.left")])]});
            var Q3;
            Q3=makeQuery(id+"F50.opExtrude","CAP_EDGE",EDGE,{"disambiguationData":[OSD([sQuery(id+"F49.wireOp",EDGE,"E107.right")])],"isStart":false});
            var Q4;
            Q4=makeQuery(id+"F50.opExtrude","CAP_EDGE",EDGE,{"disambiguationData":[OSD([sQuery(id+"F49.wireOp",EDGE,"E107.left")])],"isStart":false});
            var Q5;
            Q5=makeQuery(id+"F52.opExtrude","CAP_EDGE",EDGE,{"disambiguationData":[OSD([sQuery(id+"F51.wireOp",EDGE,"E108.right")])],"isStart":false});
            var Q6;
            Q6=makeQuery(id+"F52.opExtrude","CAP_EDGE",EDGE,{"disambiguationData":[OSD([sQuery(id+"F51.wireOp",EDGE,"E108.left")])],"isStart":false});
            var Q7;
            Q7=makeQuery(id+"F37.opExtrude","SWEPT_EDGE",EDGE,{"disambiguationData":[OSD([sQuery(id+"F35.wireOp",EDGE,"E69.top"),sQuery(id+"F35.wireOp",EDGE,"E69.left")])]});
            var Q8;
            Q8=makeQuery(id+"F45.boolean.opBoolean","COPY",EDGE,{"derivedFrom":makeQuery(id+"F45.opExtrude","SWEPT_EDGE",EDGE,{"disambiguationData":[OSD([sQuery(id+"F35.wireOp",EDGE,"E69.top"),sQuery(id+"F44.wireOp",EDGE,"E100.bottom"),sQuery(id+"F44.wireOp",EDGE,"E100.right")])]})});
            var Q9;
            Q9=makeQuery(id+"F55.opChamfer","BLEND_EDGE",EDGE,{"blendedFrom":[makeQuery(id+"F52.opExtrude","CAP_EDGE",EDGE,{"disambiguationData":[OSD([sQuery(id+"F51.wireOp",EDGE,"E108.bottom")])],"isStart":false}),makeQuery(id+"F52.opExtrude","SWEPT_FACE",FACE,{"disambiguationData":[OSD([sQuery(id+"F51.wireOp",EDGE,"E108.right")])]})],"blendedInto":[makeQuery(id+"F52.opExtrude","SWEPT_FACE",FACE,{"disambiguationData":[OSD([sQuery(id+"F51.wireOp",EDGE,"E108.right")])]})]});
            var Q10;
            Q10=makeQuery(id+"F56.opChamfer","BLEND_EDGE",EDGE,{"blendedFrom":[makeQuery(id+"F50.opExtrude","CAP_EDGE",EDGE,{"disambiguationData":[OSD([sQuery(id+"F49.wireOp",EDGE,"E107.bottom")])],"isStart":false}),makeQuery(id+"F50.opExtrude","SWEPT_FACE",FACE,{"disambiguationData":[OSD([sQuery(id+"F49.wireOp",EDGE,"E107.right")])]})],"blendedInto":[makeQuery(id+"F50.opExtrude","SWEPT_FACE",FACE,{"disambiguationData":[OSD([sQuery(id+"F49.wireOp",EDGE,"E107.right")])]})]});
            var Q11;
            Q11=makeQuery(id+"F56.opChamfer","BLEND_EDGE",EDGE,{"blendedFrom":[makeQuery(id+"F50.opExtrude","CAP_EDGE",EDGE,{"disambiguationData":[OSD([sQuery(id+"F49.wireOp",EDGE,"E107.bottom")])],"isStart":false}),makeQuery(id+"F50.opExtrude","SWEPT_FACE",FACE,{"disambiguationData":[OSD([sQuery(id+"F49.wireOp",EDGE,"E107.left")])]})],"blendedInto":[makeQuery(id+"F50.opExtrude","SWEPT_FACE",FACE,{"disambiguationData":[OSD([sQuery(id+"F49.wireOp",EDGE,"E107.left")])]})]});
            var Q12;
            Q12=makeQuery(id+"F55.opChamfer","BLEND_EDGE",EDGE,{"blendedFrom":[makeQuery(id+"F52.opExtrude","CAP_EDGE",EDGE,{"disambiguationData":[OSD([sQuery(id+"F51.wireOp",EDGE,"E108.bottom")])],"isStart":false}),makeQuery(id+"F52.opExtrude","SWEPT_FACE",FACE,{"disambiguationData":[OSD([sQuery(id+"F51.wireOp",EDGE,"E108.left")])]})],"blendedInto":[makeQuery(id+"F52.opExtrude","SWEPT_FACE",FACE,{"disambiguationData":[OSD([sQuery(id+"F51.wireOp",EDGE,"E108.left")])]})]});
            fillet(context, id + "F57", {"entities" : qUnion([Q0, Q1, Q2, Q3, Q4, Q5, Q6, Q7, Q8, Q9, Q10, Q11, Q12]), "radius" : 3 * mm, "tangentPropagation" : true, "allowEdgeOverflow" : false});
        }
        {
            var Q0;
            Q0=makeQuery(id+"F39.boolean.opBoolean","COPY",FACE,{"derivedFrom":makeQuery(id+"F39.opExtrude","CAP_FACE",FACE,{"disambiguationData":[OSD([sQuery(id+"F38.wireOp",EDGE,"E70.bottom"),sQuery(id+"F38.wireOp",EDGE,"E70.top"),sQuery(id+"F38.wireOp",EDGE,"E70.left"),sQuery(id+"F38.wireOp",EDGE,"E70.right")])],"isStart":false})});
            var sketch = newSketch(context, id + "F58", { "sketchPlane" : qUnion([Q0])});
            skCircle(sketch, "E115", {"center": v(33.11, -56) * mm, "radius": 14 * mm});
            skCircle(sketch, "E116", {"center": v(33.11, -21) * mm, "radius": 14 * mm});
            skCircle(sketch, "E117", {"center": v(73.11, -56) * mm, "radius": 14 * mm});
            skCircle(sketch, "E118", {"center": v(73.11, -21) * mm, "radius": 14 * mm});
            skCircle(sketch, "E119", {"center": v(128.11, -56) * mm, "radius": 14 * mm});
            skCircle(sketch, "E120", {"center": v(168.11, -21) * mm, "radius": 14 * mm});
            skCircle(sketch, "E121", {"center": v(168.11, -56) * mm, "radius": 14 * mm});
            skCircle(sketch, "E122", {"center": v(128.11, -21) * mm, "radius": 14 * mm});
            skSolve(sketch);
        }
        {
            var Q0;
            Q0=qSketchRegion(id+"F58",true);
            extrude(context, id + "F59", {"entities" : qUnion([Q0]), "operationType" : NewBodyOperationType.REMOVE, "oppositeDirection" : true, "depth" : 2 * mm, "offsetDistance" : 25 * mm});
        }
        {
            var Q0;
            {var subQ3=sQuery(id+"F49.wireOp",EDGE,"E107.bottom");Q0=makeQuery(id+"F49.imprint","IMPRINT",FACE,{"disambiguationData":[TD([[makeQuery(id+"F49.imprint","IMPRINT",EDGE,{"derivedFrom":subQ3}),-1.0]])]});}
            var sketch = newSketch(context, id + "F60", { "sketchPlane" : qUnion([Q0])});
            skCircle(sketch, "E123", {"center": v(96.11, 77.5) * mm, "radius": 14 * mm});
            skSolve(sketch);
        }
        {
            var Q0;
            Q0=qSketchRegion(id+"F60",true);
            extrude(context, id + "F61", {"entities" : qUnion([Q0]), "operationType" : NewBodyOperationType.REMOVE, "oppositeDirection" : true, "depth" : 2 * mm, "offsetDistance" : 25 * mm});
        }
        {
            var Q0;
            Q0=makeQuery(id+"F39.boolean.opBoolean","COPY",FACE,{"derivedFrom":makeQuery(id+"F39.opExtrude","SWEPT_FACE",FACE,{"disambiguationData":[OSD([sQuery(id+"F38.wireOp",EDGE,"E70.right")])]})});
            var sketch = newSketch(context, id + "F62", { "sketchPlane" : qUnion([Q0])});
            skCircle(sketch, "E124", {"center": v(69.5, 77.5) * mm, "radius": 14 * mm});
            skCircle(sketch, "E125", {"center": v(25, 77.5) * mm, "radius": 14 * mm});
            skSolve(sketch);
        }
        {
            var Q0;
            Q0=qSketchRegion(id+"F62",true);
            extrude(context, id + "F63", {"entities" : qUnion([Q0]), "operationType" : NewBodyOperationType.REMOVE, "oppositeDirection" : true, "depth" : 4 * mm, "offsetDistance" : 25 * mm});
        }
        {
            var Q0;
            {var subQ0=sQuery(id+"F49.wireOp",EDGE,"E107.top");Q0=makeQuery(id+"F49.imprint","IMPRINT",FACE,{"disambiguationData":[TD([[makeQuery(id+"F49.imprint","IMPRINT",EDGE,{"derivedFrom":subQ0}),-1.0]])]});}
            var sketch = newSketch(context, id + "F64", { "sketchPlane" : qUnion([Q0])});
            skCircle(sketch, "E126", {"center": v(98.61, 42) * mm, "radius": 1.75 * mm});
            skSolve(sketch);
        }
        {
            var Q0;
            Q0=qSketchRegion(id+"F64",true);
            extrude(context, id + "F65", {"entities" : qUnion([Q0]), "operationType" : NewBodyOperationType.REMOVE, "endBound" : BoundingType.THROUGH_ALL, "depth" : 25 * mm, "offsetDistance" : 25 * mm});
        }
        {
            var Q0;
            Q0=makeQuery(id+"F50.opExtrude","SWEPT_EDGE",EDGE,{"disambiguationData":[OSD([sQuery(id+"F49.wireOp",EDGE,"E107.top"),sQuery(id+"F49.wireOp",EDGE,"E107.left")])]});
            var Q1;
            Q1=makeQuery(id+"F52.opExtrude","SWEPT_EDGE",EDGE,{"disambiguationData":[OSD([sQuery(id+"F51.wireOp",EDGE,"E108.top"),sQuery(id+"F51.wireOp",EDGE,"E108.left")])]});
            fillet(context, id + "F66", {"entities" : qUnion([Q0, Q1]), "radius" : 5 * mm, "tangentPropagation" : true, "allowEdgeOverflow" : false});
        }
        {
            var Q0;
            Q0=makeQuery(id+"F46.imprint","IMPRINT",FACE,{"disambiguationData":[TD([[makeQuery(id+"F46.imprint","IMPRINT",EDGE,{"derivedFrom":sQuery(id+"F46.wireOp",EDGE,"E101")}),-1.0]])]});
            var sketch = newSketch(context, id + "F67", { "sketchPlane" : qUnion([Q0])});
            skLineSegment(sketch, "E127.bottom", {"start": v(0, 94.5) * mm, "end": v(7, 94.5) * mm});
            skLineSegment(sketch, "E127.top", {"start": v(0, 0) * mm, "end": v(7, 0) * mm});
            skLineSegment(sketch, "E127.left", {"start": v(0, 94.5) * mm, "end": v(0, 0) * mm});
            skLineSegment(sketch, "E127.right", {"start": v(7, 94.5) * mm, "end": v(7, 0) * mm});
            skLineSegment(sketch, "E128.bottom", {"start": v(7, 94.5) * mm, "end": v(58, 94.5) * mm});
            skLineSegment(sketch, "E128.top", {"start": v(7, 89.5) * mm, "end": v(58, 89.5) * mm});
            skLineSegment(sketch, "E128.left", {"start": v(7, 94.5) * mm, "end": v(7, 89.5) * mm});
            skLineSegment(sketch, "E128.right", {"start": v(58, 94.5) * mm, "end": v(58, 89.5) * mm});
            skLineSegment(sketch, "E129.bottom", {"start": v(7, 0) * mm, "end": v(58, 0) * mm});
            skLineSegment(sketch, "E129.top", {"start": v(7, 5) * mm, "end": v(58, 5) * mm});
            skLineSegment(sketch, "E129.left", {"start": v(7, 0) * mm, "end": v(7, 5) * mm});
            skLineSegment(sketch, "E129.right", {"start": v(58, 0) * mm, "end": v(58, 5) * mm});
            skSolve(sketch);
        }
        {
            var Q0;
            Q0=qSketchRegion(id+"F67",true);
            extrude(context, id + "F68", {"entities" : qUnion([Q0]), "depth" : 63 * mm, "offsetDistance" : 25 * mm});
        }
        {
            var Q0;
            Q0=makeQuery(id+"F68.opExtrude","CAP_EDGE",EDGE,{"disambiguationData":[OSD([sQuery(id+"F67.wireOp",EDGE,"E129.right"),sQuery(id+"F67.wireOp",EDGE,"UJTcfqSP-XtTE-oda9-0cFO-EFd9Vn1DxB2z.left")])],"isStart":false});
            var Q1;
            Q1=makeQuery(id+"F68.opExtrude","CAP_EDGE",EDGE,{"disambiguationData":[OSD([sQuery(id+"F67.wireOp",EDGE,"E128.right"),sQuery(id+"F67.wireOp",EDGE,"aQafAQoN-KdM9-0gy1-g6xU-W6zrJBISKPlm.left")])],"isStart":false});
            chamfer(context, id + "F69", {"entities" : qUnion([Q0, Q1]), "chamferType" : ChamferType.TWO_OFFSETS, "width1" : 50 * mm, "oppositeDirection" : false, "width2" : 58 * mm, "tangentPropagation" : true});
        }
        {
            var Q0;
            Q0=makeQuery(id+"F37.opExtrude","CAP_FACE",FACE,{"disambiguationData":[OSD([sQuery(id+"F35.wireOp",EDGE,"E69.bottom"),sQuery(id+"F35.wireOp",EDGE,"E69.top"),sQuery(id+"F35.wireOp",EDGE,"E69.left"),sQuery(id+"F35.wireOp",EDGE,"E69.right")])],"isStart":false});
            var sketch = newSketch(context, id + "F70", { "sketchPlane" : qUnion([Q0])});
            skLineSegment(sketch, "E130.bottom", {"start": v(58, 89.5) * mm, "end": v(48, 89.5) * mm});
            skLineSegment(sketch, "E130.top", {"start": v(58, 79.5) * mm, "end": v(48, 79.5) * mm});
            skLineSegment(sketch, "E130.left", {"start": v(58, 89.5) * mm, "end": v(58, 79.5) * mm});
            skLineSegment(sketch, "E130.right", {"start": v(48, 89.5) * mm, "end": v(48, 79.5) * mm});
            skLineSegment(sketch, "E131.bottom", {"start": v(58, 5) * mm, "end": v(48, 5) * mm});
            skLineSegment(sketch, "E131.top", {"start": v(58, 15) * mm, "end": v(48, 15) * mm});
            skLineSegment(sketch, "E131.left", {"start": v(58, 5) * mm, "end": v(58, 15) * mm});
            skLineSegment(sketch, "E131.right", {"start": v(48, 5) * mm, "end": v(48, 15) * mm});
            skLineSegment(sketch, "E132.bottom", {"start": v(7, 49.75) * mm, "end": v(17, 49.75) * mm});
            skLineSegment(sketch, "E132.top", {"start": v(7, 39.75) * mm, "end": v(17, 39.75) * mm});
            skLineSegment(sketch, "E132.left", {"start": v(7, 49.75) * mm, "end": v(7, 39.75) * mm});
            skLineSegment(sketch, "E132.right", {"start": v(17, 49.75) * mm, "end": v(17, 39.75) * mm});
            skCircle(sketch, "E133", {"center": v(53, 84.5) * mm, "radius": 2.5 * mm});
            skCircle(sketch, "E134", {"center": v(53, 10) * mm, "radius": 2.5 * mm});
            skCircle(sketch, "E135", {"center": v(12, 44.75) * mm, "radius": 2.5 * mm});
            skLineSegment(sketch, "E136.bottom", {"start": v(7, 5) * mm, "end": v(17, 5) * mm});
            skLineSegment(sketch, "E136.top", {"start": v(7, 15) * mm, "end": v(17, 15) * mm});
            skLineSegment(sketch, "E136.left", {"start": v(7, 5) * mm, "end": v(7, 15) * mm});
            skLineSegment(sketch, "E136.right", {"start": v(17, 5) * mm, "end": v(17, 15) * mm});
            skLineSegment(sketch, "E137.bottom", {"start": v(7, 89.5) * mm, "end": v(17, 89.5) * mm});
            skLineSegment(sketch, "E137.top", {"start": v(7, 79.5) * mm, "end": v(17, 79.5) * mm});
            skLineSegment(sketch, "E137.left", {"start": v(7, 89.5) * mm, "end": v(7, 79.5) * mm});
            skLineSegment(sketch, "E137.right", {"start": v(17, 89.5) * mm, "end": v(17, 79.5) * mm});
            skCircle(sketch, "E138", {"center": v(12, 10) * mm, "radius": 2.5 * mm});
            skCircle(sketch, "E139", {"center": v(12, 84.5) * mm, "radius": 2.5 * mm});
            skSolve(sketch);
        }
        {
            var Q0;
            Q0=qSketchRegion(id+"F70",true);
            extrude(context, id + "F71", {"entities" : qUnion([Q0]), "operationType" : NewBodyOperationType.ADD, "depth" : 4 * mm, "offsetDistance" : 25 * mm});
        }
        {
            var Q0;
            Q0=makeQuery(id+"F68.opExtrude","CAP_FACE",FACE,{"disambiguationData":[OSD([sQuery(id+"F67.wireOp",EDGE,"E127.bottom"),sQuery(id+"F67.wireOp",EDGE,"E127.top"),sQuery(id+"F67.wireOp",EDGE,"E127.left"),sQuery(id+"F67.wireOp",EDGE,"E127.right"),sQuery(id+"F67.wireOp",EDGE,"E128.bottom"),sQuery(id+"F67.wireOp",EDGE,"E128.top"),sQuery(id+"F67.wireOp",EDGE,"E128.right"),sQuery(id+"F67.wireOp",EDGE,"E129.bottom"),sQuery(id+"F67.wireOp",EDGE,"E129.top"),sQuery(id+"F67.wireOp",EDGE,"E129.right")])],"isStart":false});
            var sketch = newSketch(context, id + "F72", { "sketchPlane" : qUnion([Q0])});
            skLineSegment(sketch, "E140.bottom", {"start": v(0, 94.5) * mm, "end": v(10, 94.5) * mm});
            skLineSegment(sketch, "E140.top", {"start": v(0, 93.5) * mm, "end": v(10, 93.5) * mm});
            skLineSegment(sketch, "E140.left", {"start": v(0, 94.5) * mm, "end": v(0, 93.5) * mm});
            skLineSegment(sketch, "E140.right", {"start": v(10, 94.5) * mm, "end": v(10, 93.5) * mm});
            skSolve(sketch);
        }
        {
            var Q0;
            Q0=qSketchRegion(id+"F72",true);
            var Q1;
            Q1=makeQuery(id+"F71.boolean.opBoolean","MERGE",FACE,{"derivedFrom":[makeQuery(id+"F68.opExtrude","CAP_FACE",FACE,{"disambiguationData":[OSD([sQuery(id+"F67.wireOp",EDGE,"E127.bottom"),sQuery(id+"F67.wireOp",EDGE,"E127.top"),sQuery(id+"F67.wireOp",EDGE,"E127.left"),sQuery(id+"F67.wireOp",EDGE,"E127.right"),sQuery(id+"F67.wireOp",EDGE,"E128.bottom"),sQuery(id+"F67.wireOp",EDGE,"E128.top"),sQuery(id+"F67.wireOp",EDGE,"E128.right"),sQuery(id+"F67.wireOp",EDGE,"E129.bottom"),sQuery(id+"F67.wireOp",EDGE,"E129.top"),sQuery(id+"F67.wireOp",EDGE,"E129.right")])],"isStart":true}),makeQuery(id+"F71.opExtrude","CAP_FACE",FACE,{"disambiguationData":[OSD([sQuery(id+"F70.wireOp",EDGE,"E130.bottom"),sQuery(id+"F70.wireOp",EDGE,"E130.top"),sQuery(id+"F70.wireOp",EDGE,"E130.left"),sQuery(id+"F70.wireOp",EDGE,"E130.right"),sQuery(id+"F70.wireOp",EDGE,"E133")])],"isStart":true}),makeQuery(id+"F71.opExtrude","CAP_FACE",FACE,{"disambiguationData":[OSD([sQuery(id+"F70.wireOp",EDGE,"E131.bottom"),sQuery(id+"F70.wireOp",EDGE,"E131.top"),sQuery(id+"F70.wireOp",EDGE,"E131.left"),sQuery(id+"F70.wireOp",EDGE,"E131.right"),sQuery(id+"F70.wireOp",EDGE,"E134")])],"isStart":true}),makeQuery(id+"F71.opExtrude","CAP_FACE",FACE,{"disambiguationData":[OSD([sQuery(id+"F70.wireOp",EDGE,"E132.bottom"),sQuery(id+"F70.wireOp",EDGE,"E132.top"),sQuery(id+"F70.wireOp",EDGE,"E132.left"),sQuery(id+"F70.wireOp",EDGE,"E132.right"),sQuery(id+"F70.wireOp",EDGE,"E135")])],"isStart":true}),makeQuery(id+"F71.opExtrude","CAP_FACE",FACE,{"disambiguationData":[OSD([sQuery(id+"F70.wireOp",EDGE,"E136.bottom"),sQuery(id+"F70.wireOp",EDGE,"E136.top"),sQuery(id+"F70.wireOp",EDGE,"E136.left"),sQuery(id+"F70.wireOp",EDGE,"E136.right"),sQuery(id+"F70.wireOp",EDGE,"E138")])],"isStart":true}),makeQuery(id+"F71.opExtrude","CAP_FACE",FACE,{"disambiguationData":[OSD([sQuery(id+"F70.wireOp",EDGE,"E137.bottom"),sQuery(id+"F70.wireOp",EDGE,"E137.top"),sQuery(id+"F70.wireOp",EDGE,"E137.left"),sQuery(id+"F70.wireOp",EDGE,"E137.right"),sQuery(id+"F70.wireOp",EDGE,"E139")])],"isStart":true})]});
            extrude(context, id + "F73", {"entities" : qUnion([Q0]), "operationType" : NewBodyOperationType.REMOVE, "endBound" : BoundingType.UP_TO_SURFACE, "oppositeDirection" : true, "depth" : 25 * mm, "endBoundEntityFace" : qUnion([Q1]), "offsetDistance" : 25 * mm});
        }
        {
            var Q0;
            Q0=makeQuery(id+"F68.opExtrude","SWEPT_FACE",FACE,{"disambiguationData":[OSD([sQuery(id+"F67.wireOp",EDGE,"E127.left")])]});
            var sketch = newSketch(context, id + "F74", { "sketchPlane" : qUnion([Q0])});
            skCircle(sketch, "E141", {"center": v(-68.75, 134.5) * mm, "radius": 12.5 * mm});
            skCircle(sketch, "E142", {"center": v(-24.75, 134.5) * mm, "radius": 12.5 * mm});
            skCircle(sketch, "E143", {"center": v(-56.25, 122) * mm, "radius": 1.75 * mm});
            skCircle(sketch, "E144", {"center": v(-37.25, 122) * mm, "radius": 1.75 * mm});
            skCircle(sketch, "E145", {"center": v(-12.25, 122) * mm, "radius": 1.75 * mm});
            skCircle(sketch, "E146", {"center": v(-12.25, 147) * mm, "radius": 1.75 * mm});
            skCircle(sketch, "E147", {"center": v(-56.25, 147) * mm, "radius": 1.75 * mm});
            skCircle(sketch, "E148", {"center": v(-81.25, 147) * mm, "radius": 1.75 * mm});
            skCircle(sketch, "E149", {"center": v(-37.25, 147) * mm, "radius": 1.75 * mm});
            skCircle(sketch, "E150", {"center": v(-81.25, 122) * mm, "radius": 1.75 * mm});
            skSolve(sketch);
        }
        {
            var Q0;
            Q0=qSketchRegion(id+"F74",true);
            extrude(context, id + "F75", {"entities" : qUnion([Q0]), "operationType" : NewBodyOperationType.REMOVE, "oppositeDirection" : true, "depth" : 25 * mm, "offsetDistance" : 25 * mm});
        }
        {
            var Q0;
            Q0=makeQuery(id+"F73.boolean.opBoolean","COPY",EDGE,{"derivedFrom":makeQuery(id+"F73.opExtrude","SWEPT_EDGE",EDGE,{"disambiguationData":[OSD([sQuery(id+"F67.wireOp",EDGE,"E127.left"),sQuery(id+"F72.wireOp",EDGE,"E140.top"),sQuery(id+"F72.wireOp",EDGE,"E140.left")])]})});
            var Q1;
            Q1=makeQuery(id+"F68.opExtrude","SWEPT_EDGE",EDGE,{"disambiguationData":[OSD([sQuery(id+"F67.wireOp",EDGE,"E127.top"),sQuery(id+"F67.wireOp",EDGE,"E127.left")])]});
            var Q2;
            Q2=makeQuery(id+"F73.boolean.opBoolean","COPY",EDGE,{"derivedFrom":makeQuery(id+"F73.opExtrude","SWEPT_EDGE",EDGE,{"disambiguationData":[OSD([sQuery(id+"F72.wireOp",EDGE,"E140.bottom"),sQuery(id+"F72.wireOp",EDGE,"E140.right")])]})});
            var Q3;
            Q3=makeQuery(id+"F71.opExtrude","SWEPT_EDGE",EDGE,{"disambiguationData":[OSD([sQuery(id+"F70.wireOp",EDGE,"E137.top"),sQuery(id+"F70.wireOp",EDGE,"E137.right")])]});
            var Q4;
            Q4=makeQuery(id+"F71.opExtrude","SWEPT_EDGE",EDGE,{"disambiguationData":[OSD([sQuery(id+"F70.wireOp",EDGE,"E130.top"),sQuery(id+"F70.wireOp",EDGE,"E130.left")])]});
            var Q5;
            Q5=makeQuery(id+"F71.opExtrude","SWEPT_EDGE",EDGE,{"disambiguationData":[OSD([sQuery(id+"F70.wireOp",EDGE,"E130.top"),sQuery(id+"F70.wireOp",EDGE,"E130.right")])]});
            var Q6;
            Q6=makeQuery(id+"F71.opExtrude","SWEPT_EDGE",EDGE,{"disambiguationData":[OSD([sQuery(id+"F70.wireOp",EDGE,"E132.bottom"),sQuery(id+"F70.wireOp",EDGE,"E132.right")])]});
            var Q7;
            Q7=makeQuery(id+"F71.opExtrude","SWEPT_EDGE",EDGE,{"disambiguationData":[OSD([sQuery(id+"F70.wireOp",EDGE,"E132.top"),sQuery(id+"F70.wireOp",EDGE,"E132.right")])]});
            var Q8;
            Q8=makeQuery(id+"F71.opExtrude","SWEPT_EDGE",EDGE,{"disambiguationData":[OSD([sQuery(id+"F70.wireOp",EDGE,"E131.top"),sQuery(id+"F70.wireOp",EDGE,"E131.left")])]});
            var Q9;
            Q9=makeQuery(id+"F71.opExtrude","SWEPT_EDGE",EDGE,{"disambiguationData":[OSD([sQuery(id+"F70.wireOp",EDGE,"E131.top"),sQuery(id+"F70.wireOp",EDGE,"E131.right")])]});
            var Q10;
            Q10=makeQuery(id+"F71.opExtrude","SWEPT_EDGE",EDGE,{"disambiguationData":[OSD([sQuery(id+"F70.wireOp",EDGE,"E136.top"),sQuery(id+"F70.wireOp",EDGE,"E136.right")])]});
            fillet(context, id + "F76", {"entities" : qUnion([Q0, Q1, Q2, Q3, Q4, Q5, Q6, Q7, Q8, Q9, Q10]), "radius" : 3 * mm, "tangentPropagation" : true, "allowEdgeOverflow" : false});
        }
    });
